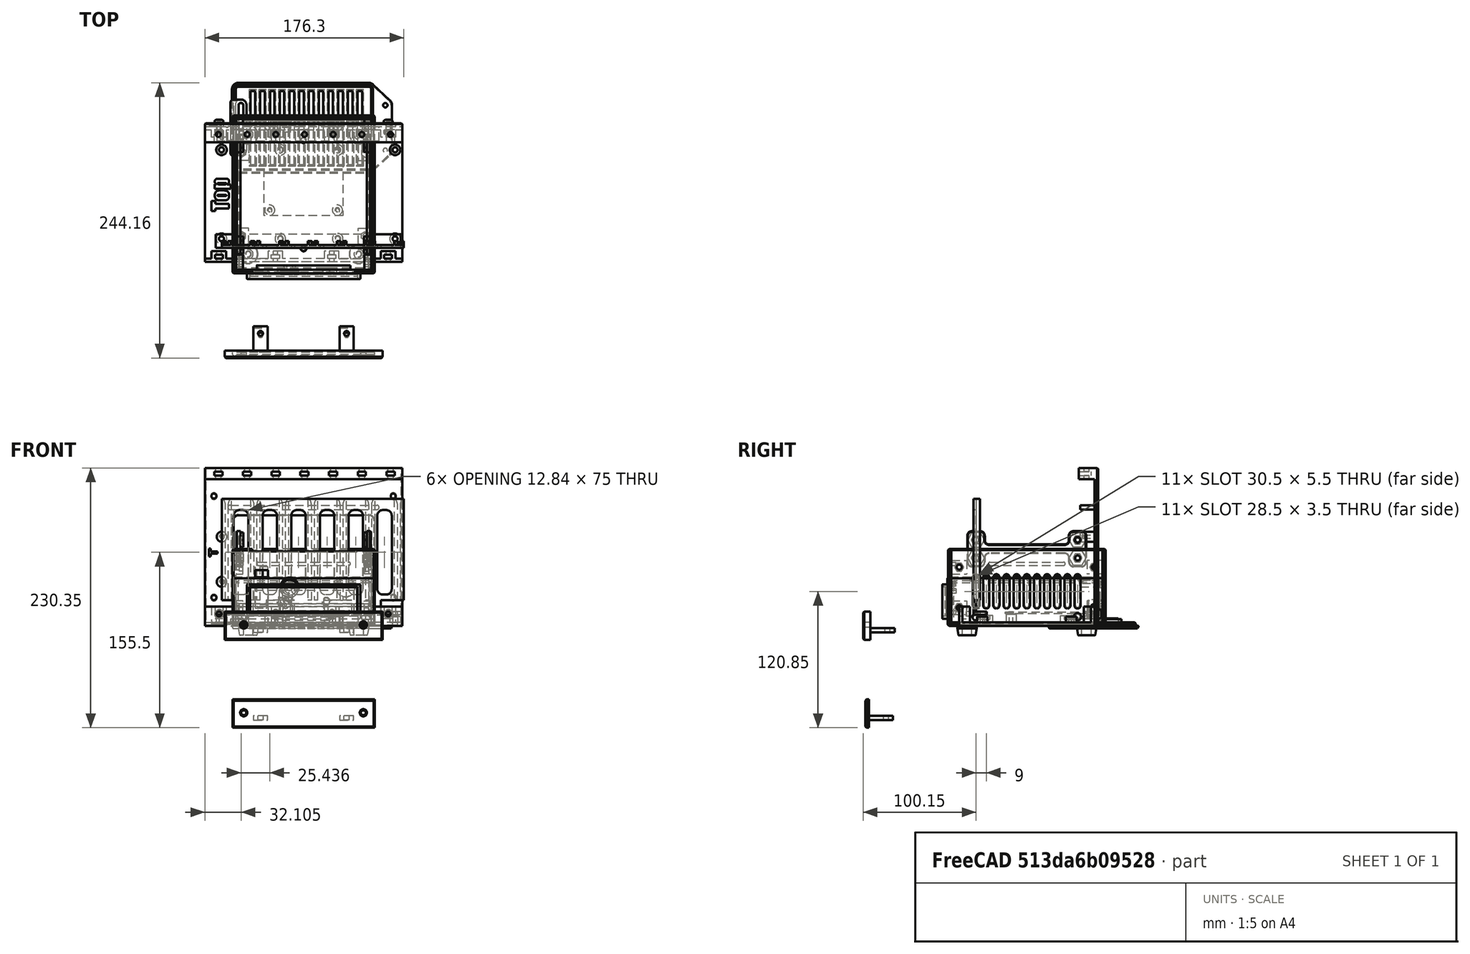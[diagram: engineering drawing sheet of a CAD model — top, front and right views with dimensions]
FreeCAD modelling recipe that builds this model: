
FCSTD DOCUMENT  (FreeCAD 0.20R29603 (Git))
Label: Assembly Model
License: All rights reserved
LicenseURL: http://en.wikipedia.org/wiki/All_rights_reserved
objects: Sketcher::SketchObject×60, PartDesign::Pocket×32, PartDesign::Pad×28, PartDesign::Chamfer×25, PartDesign::Body×14, PartDesign::Mirrored×12, Part::Feature×8, App::Part×6, PartDesign::Fillet×6, Part::FeaturePython×5, Part::Mirroring×4, App::DocumentObjectGroup×4, PartDesign::ShapeBinder×2, PartDesign::LinearPattern×1, PartDesign::Revolution×1, PartDesign::Thickness×1, Part::Part2DObjectPython×1
note: 293 computed .brp shape members not serialized (recipe doc carries the construction recipe); baked Part::Feature solids carry a one-line shape summary decoded from their .brp

FEATURE [Part::Feature] Part__Feature001  label="Guide"
  Placement = pos=(4.1875,39.425,9.65) rot=(0,0,1;0rad)
  shape: bbox 166.6 x 12 x 103 mm, 167 faces (baked)
FEATURE [Part::Mirroring] Part__Mirroring001  label="Guide (Mirror #2)"
  Base = (0,0,0)
  Normal = (0,1,0)
  Source = -> Part__Feature001
FEATURE [Part::Feature] Part__Feature004  label="M4 X 10 Pan Hd Pozi"
  Placement = pos=(-75,-63.15,10.5) rot=(1,0,0;1.5708rad)
  shape: bbox 8.444 x 13.1 x 8.444 mm, 27 faces (baked)
FEATURE [Part::FeaturePython] Array  # Draft array (typed FeaturePython)
  Angle = 360
  ArrayType = 0
  Axis = (0,0,1)
  Base = -> Part__Feature004
  Center = (0,0,0)
  Fuse = false
  IntervalAxis = (0,0,0)
  IntervalX = (50,0,0)
  IntervalY = (0,1,0)
  IntervalZ = (0,0,1)
  NumberPolar = 1
  NumberX = 4
  NumberY = 1
  NumberZ = 1
FEATURE [Part::Mirroring] Part__Mirroring003  label="Side panel retaining nuts"
  Base = (0,0,0)
  Normal = (0,1,0)
  Source = -> Array
FEATURE [Part::Feature] Part__Feature005  label="M4 Nut"
  Placement = pos=(-75,-55.375,10.5) rot=(1,0,0;0rad)
  shape: bbox 7.66 x 3.2 x 7.66 mm, 19 faces (baked)
FEATURE [Part::Feature] Part__Feature006  label="Sideplate"
  Placement = pos=(-8e-15,-63.1,0) rot=(0,0.707107,0.707107;3.14159rad)
  shape: bbox 175 x 17 x 140 mm, 120 faces (baked)
FEATURE [Part::Mirroring] Part__Mirroring  label="Sideplate (Mirror #5)"
  Base = (0,0,0)
  Normal = (0,1,0)
  Source = -> Part__Feature006
FEATURE [Part::Feature] Part__Feature007  label="Vented_cover"
  shape: bbox 142 x 80.02 x 8.7 mm, 193 faces (baked)
FEATURE [Part::Feature] Part__Feature008  label="Tab"
  shape: bbox 14.5 x 50 x 2.7 mm, 17 faces (baked)
FEATURE [App::DocumentObjectGroup] Group  label="Side-cover assy"
  Group = -> [Part__Feature007,Part__Feature008]
FEATURE [App::Part] Part  label="Side Cover Assy"
  Group = -> [Part__Feature008,Part__Feature007,Group]
  Origin = -> Origin002
  Placement = pos=(-7.7e-15,-63,0) rot=(0,0.707107,0.707107;3.14159rad)
FEATURE [Part::Feature] Part__Feature009  label="Tab001"
  shape: bbox 14.5 x 50 x 2.7 mm, 17 faces (baked)
FEATURE [Part::Feature] Part__Feature010  label="Vented_cover001"
  shape: bbox 142 x 80.02 x 8.7 mm, 193 faces (baked)
FEATURE [App::DocumentObjectGroup] Group001  label="Side-cover assy001"
  Group = -> [Part__Feature010,Part__Feature009]
FEATURE [App::Part] Part001  label="Side Cover Assy 2"
  Group = -> [Part__Feature009,Part__Feature010,Group001]
  Origin = -> Origin003
  Placement = pos=(7.7e-15,63,118) rot=(0,0.707107,-0.707107;3.14159rad)
FEATURE [Part::FeaturePython] Array001  label="Nuts for sideplate"  # Draft array (typed FeaturePython)
  Angle = 360
  ArrayType = 0
  Axis = (0,0,1)
  Base = -> Part__Feature005
  Center = (0,0,0)
  Fuse = false
  IntervalAxis = (0,0,0)
  IntervalX = (50,0,0)
  IntervalY = (0,1,0)
  IntervalZ = (0,0,1)
  NumberPolar = 1
  NumberX = 4
  NumberY = 1
  NumberZ = 1
FEATURE [Part::Mirroring] Part__Mirroring004  label="Nuts for sideplate (Mirror #5)"
  Base = (0,0,0)
  Normal = (0,1,0)
  Source = -> Array001
FEATURE [Sketcher::SketchObject] Sketch001  label="Base plate spec"
  FullyConstrained = false
  MapMode = 5
  Support = -> [XY_Plane005]
  sketch-geometry (12):
    g0: LineSegment StartX=-63 StartY=67 StartZ=0 EndX=63 EndY=67 EndZ=0
    g1: LineSegment StartX=63 StartY=67 StartZ=0 EndX=63 EndY=-67 EndZ=0
    g2: LineSegment StartX=63 StartY=-67 StartZ=0 EndX=-63 EndY=-67 EndZ=0
    g3: LineSegment StartX=-63 StartY=-67 StartZ=0 EndX=-63 EndY=67 EndZ=0
    g4: Circle CenterX=-49 CenterY=53 CenterZ=0 NormalX=0 NormalY=0 NormalZ=1 AngleXU=0 Radius=2.4
    g5: Circle CenterX=49 CenterY=53 CenterZ=0 NormalX=0 NormalY=0 NormalZ=1 AngleXU=0 Radius=2.4
    g6: Circle CenterX=-49 CenterY=-53 CenterZ=0 NormalX=0 NormalY=0 NormalZ=1 AngleXU=0 Radius=2.4
    g7: Circle CenterX=49 CenterY=-53 CenterZ=0 NormalX=0 NormalY=0 NormalZ=1 AngleXU=0 Radius=2.4
    g8: Circle CenterX=55 CenterY=37 CenterZ=0 NormalX=0 NormalY=0 NormalZ=1 AngleXU=0 Radius=2.4
    g9: Circle CenterX=-55 CenterY=37 CenterZ=0 NormalX=0 NormalY=0 NormalZ=1 AngleXU=0 Radius=2.4
    g10: Circle CenterX=-55 CenterY=-37 CenterZ=0 NormalX=0 NormalY=0 NormalZ=1 AngleXU=0 Radius=2.4
    g11: Circle CenterX=55 CenterY=-37 CenterZ=0 NormalX=0 NormalY=0 NormalZ=1 AngleXU=0 Radius=2.4
  constraints (28):
    c: Coincident(g0,g1)
    c: Coincident(g1,g2)
    c: Coincident(g2,g3)
    c: Coincident(g3,g0)
    c: Horizontal(g2)
    c: Vertical(g1)
    c: Symmetric(g0,g0,g-2)
    c: Symmetric(g0,g2,g-1)
    c: Distance(g0) = 126
    c: Distance(g3) = 134
    c: Radius(g4) = 2.4
    c: Equal(g4,g5)
    c: Equal(g4,g6)
    c: Equal(g4,g7)
    c: Symmetric(g4,g5,g-2)
    c: Symmetric(g4,g6,g-1)
    c: Symmetric(g7,g6,g-2)
    c: Distance(g4,g5) = 98
    c: DistanceY(g6,g4) = 106
    c: Symmetric(g10,g11,g-2)
    c: Symmetric(g9,g10,g-1)
    c: Symmetric(g9,g8,g-2)
    c: Radius(g9) = 2.4
    c: Equal(g9,g8)
    c: Equal(g9,g11)
    c: Equal(g9,g10)
    c: DistanceX(g0,g9) = 8
    c: DistanceY(g9,g0) = 30
FEATURE [PartDesign::Pad] Pad  label="Make base plate"
  AllowMultiFace = false
  Direction = (1,1,1)
  Length = 3
  Length2 = 100
  Profile = -> Sketch001
  Type = 0
FEATURE [Sketcher::SketchObject] Sketch002  label="Sideplate spec"
  FullyConstrained = false
  MapMode = 5
  Placement = pos=(0,0,0) rot=(1,0,0;1.5708rad)
  Support = -> [XZ_Plane006]
  sketch-geometry (4):
    g0: LineSegment StartX=-60 StartY=3.05 StartZ=0 EndX=-63 EndY=3.05 EndZ=0
    g1: LineSegment StartX=-63 StartY=3.05 StartZ=0 EndX=-63 EndY=68.05 EndZ=0
    g2: LineSegment StartX=-63 StartY=68.05 StartZ=0 EndX=-60 EndY=68.05 EndZ=0
    g3: LineSegment StartX=-60 StartY=68.05 StartZ=0 EndX=-60 EndY=3.05 EndZ=0
  constraints (12):
    c: Coincident(g0,g1)
    c: Coincident(g1,g2)
    c: Coincident(g2,g3)
    c: Horizontal(g0)
    c: Horizontal(g2)
    c: Vertical(g3)
    c: Vertical(g1)
    c: Distance(g1) = 65
    c: Distance(g2) = 3
    c: DistanceX(g0) = -63
    c: DistanceY(g0) = 3.05
    c: Coincident(g3,g0)
FEATURE [PartDesign::Pad] Pad001  label="Make sideplate"
  AllowMultiFace = false
  Direction = (1,1,1)
  Length = 134
  Length2 = 100
  Midplane = true
  Placement = pos=(0,0,0) rot=(1,0,0;1.5708rad)
  Profile = -> Sketch002
  Type = 0
FEATURE [Sketcher::SketchObject] Sketch003  label="Screwtab spec"
  ExternalGeometry = -> [Pad001]
  FullyConstrained = false
  MapMode = 5
  Placement = pos=(0,0,3.05) rot=(1,0,0;3.14159rad)
  Support = -> [Pad001]
  sketch-geometry (13):
    g0: LineSegment StartX=-60 StartY=44 StartZ=0 EndX=-48.5 EndY=44 EndZ=0
    g1: LineSegment StartX=-48.5 StartY=44 StartZ=0 EndX=-48.5 EndY=30 EndZ=0
    g2: LineSegment StartX=-48.5 StartY=30 StartZ=0 EndX=-60 EndY=30 EndZ=0
    g3: LineSegment StartX=-60 StartY=30 StartZ=0 EndX=-60 EndY=44 EndZ=0
    g4: LineSegment StartX=-60 StartY=37 StartZ=0 EndX=-48.5 EndY=37 EndZ=0
    g5: Circle CenterX=-55 CenterY=37 CenterZ=0 NormalX=0 NormalY=0 NormalZ=1 AngleXU=0 Radius=2.4
    g6: LineSegment StartX=-51.5 StartY=34.9793 StartZ=0 EndX=-51.5 EndY=39.0207 EndZ=0
    g7: LineSegment StartX=-51.5 StartY=39.0207 StartZ=0 EndX=-55 EndY=41.0415 EndZ=0
    g8: LineSegment StartX=-55 StartY=41.0415 StartZ=0 EndX=-58.5 EndY=39.0207 EndZ=0
    g9: LineSegment StartX=-58.5 StartY=39.0207 StartZ=0 EndX=-58.5 EndY=34.9793 EndZ=0
    g10: LineSegment StartX=-58.5 StartY=34.9793 StartZ=0 EndX=-55 EndY=32.9585 EndZ=0
    g11: LineSegment StartX=-55 StartY=32.9585 StartZ=0 EndX=-51.5 EndY=34.9793 EndZ=0
    g12: Circle CenterX=-55 CenterY=37 CenterZ=0 NormalX=0 NormalY=0 NormalZ=1 AngleXU=0 Radius=4.04145
  constraints (34):
    c: Coincident(g0,g1)
    c: Coincident(g1,g2)
    c: Coincident(g2,g3)
    c: Coincident(g3,g0)
    c: Horizontal(g0)
    c: Horizontal(g2)
    c: Vertical(g1)
    c: Vertical(g3)
    c: Perpendicular(g4,g1) = 4.71239
    c: PointOnObject(g4,g3)
    c: PointOnObject(g5,g4)
    c: PointOnObject(g0,g-3)
    c: Symmetric(g0,g1,g4)
    c: DistanceY(g5,g-3) = 30
    c: DistanceX(g-4,g5) = 8
    c: Coincident(g6,g7)
    c: Coincident(g7,g8)
    c: Coincident(g8,g9)
    c: Coincident(g9,g10)
    c: Coincident(g10,g11)
    c: Coincident(g11,g6)
    c: Equal(g6, g7-g11) x5
    c: PointOnObject(g6,g12)
    c: PointOnObject(g7,g12)
    c: PointOnObject(g8,g12)
    c: PointOnObject(g9,g12)
    c: PointOnObject(g10,g12)
    c: PointOnObject(g11,g12)
    c: Coincident(g12,g5)
    c: Vertical(g6)
    c: DistanceX(g9,g6) = 7
    c: DistanceX(g6,g0) = 3
    c: Distance(g1) = 14
    c: Radius(g5) = 2.4
FEATURE [PartDesign::Pad] Pad002  label="Add screwtab"
  AllowMultiFace = false
  BaseFeature = -> Pad001
  Direction = (1,1,1)
  Length = 6
  Length2 = 100
  Placement = pos=(0,0,0) rot=(1,0,0;1.5708rad)
  Profile = -> Sketch003
  Reversed = true
  Type = 0
FEATURE [PartDesign::Mirrored] Mirrored  label="Mirrored screwtab"
  BaseFeature = -> Pad002
  MirrorPlane = -> XZ_Plane006
  Originals = -> [Pad002]
  Placement = pos=(0,0,0) rot=(1,0,0;1.5708rad)
FEATURE [Sketcher::SketchObject] Sketch004  label="nut trap spec"
  ExternalGeometry = -> [Mirrored]
  FullyConstrained = false
  MapMode = 5
  Placement = pos=(0,-2e-15,9.05) rot=(0,0,1;3.14159rad)
  Support = -> [Mirrored]
  sketch-geometry (7):
    g0: LineSegment StartX=58.55 StartY=34.9504 StartZ=0 EndX=58.55 EndY=39.0496 EndZ=0
    g1: LineSegment StartX=58.55 StartY=39.0496 StartZ=0 EndX=55 EndY=41.0992 EndZ=0
    g2: LineSegment StartX=55 StartY=41.0992 StartZ=0 EndX=51.45 EndY=39.0496 EndZ=0
    g3: LineSegment StartX=51.45 StartY=39.0496 StartZ=0 EndX=51.45 EndY=34.9504 EndZ=0
    g4: LineSegment StartX=51.45 StartY=34.9504 StartZ=0 EndX=55 EndY=32.9008 EndZ=0
    g5: LineSegment StartX=55 StartY=32.9008 StartZ=0 EndX=58.55 EndY=34.9504 EndZ=0
    g6: Circle CenterX=55 CenterY=37 CenterZ=0 NormalX=0 NormalY=0 NormalZ=1 AngleXU=0 Radius=4.09919
  constraints (16):
    c: Coincident(g0,g1)
    c: Coincident(g1,g2)
    c: Coincident(g2,g3)
    c: Coincident(g3,g4)
    c: Coincident(g4,g5)
    c: Coincident(g5,g0)
    c: Equal(g0, g1-g5) x5
    c: PointOnObject(g0,g6)
    c: PointOnObject(g1,g6)
    c: PointOnObject(g2,g6)
    c: PointOnObject(g3,g6)
    c: PointOnObject(g4,g6)
    c: PointOnObject(g5,g6)
    c: Coincident(g6,g-3)
    c: Vertical(g0)
    c: Distance(g0,g3) = 7.1
FEATURE [PartDesign::Pocket] Pocket  label="Add nut trap"
  AllowMultiFace = false
  BaseFeature = -> Mirrored
  Direction = (1,1,1)
  Length = 3.5
  Length2 = 100
  Placement = pos=(0,0,0) rot=(1,0,0;1.5708rad)
  Profile = -> Sketch004
  Type = 0
FEATURE [PartDesign::Mirrored] Mirrored001  label="Mirrored nut-trap"
  BaseFeature = -> Pocket
  MirrorPlane = -> XZ_Plane006
  Originals = -> [Pocket]
  Placement = pos=(0,0,0) rot=(1,0,0;1.5708rad)
FEATURE [Sketcher::SketchObject] Sketch005  label="PCB Base"
  FullyConstrained = false
  MapMode = 5
  Support = -> [XY_Plane007]
  sketch-geometry (11):
    g0: LineSegment StartX=-50 StartY=35 StartZ=0 EndX=35 EndY=35 EndZ=0
    g1: LineSegment StartX=35 StartY=35 StartZ=0 EndX=35 EndY=-35 EndZ=0
    g2: LineSegment StartX=35 StartY=-35 StartZ=0 EndX=-50 EndY=-35 EndZ=0
    g3: LineSegment StartX=-50 StartY=-35 StartZ=0 EndX=-50 EndY=35 EndZ=0
    g4: Circle CenterX=-45 CenterY=-30 CenterZ=0 NormalX=0 NormalY=0 NormalZ=1 AngleXU=0 Radius=2.1
    g5: Circle CenterX=30 CenterY=-30 CenterZ=0 NormalX=0 NormalY=0 NormalZ=1 AngleXU=0 Radius=2.1
    g6: Circle CenterX=-45 CenterY=30 CenterZ=0 NormalX=0 NormalY=0 NormalZ=1 AngleXU=0 Radius=2.1
    g7: Circle CenterX=30 CenterY=30 CenterZ=0 NormalX=0 NormalY=0 NormalZ=1 AngleXU=0 Radius=2.1
    g8: LineSegment StartX=-7.5 StartY=35 StartZ=0 EndX=-7.5 EndY=-35 EndZ=0
    g9: LineSegment StartX=-50 StartY=-3.1e-15 StartZ=0 EndX=35 EndY=2.1e-15 EndZ=0
    g10: GeomPoint X=0 Y=0 Z=0
  constraints (28):
    c: Coincident(g0,g1)
    c: Coincident(g1,g2)
    c: Coincident(g2,g3)
    c: Coincident(g3,g0)
    c: Horizontal(g0)
    c: Horizontal(g2)
    c: Vertical(g1)
    c: Vertical(g3)
    c: Distance(g3) = 70
    c: Distance(g0) = 85
    c: Radius(g6) = 2.1
    c: Equal(g6,g7)
    c: Equal(g6,g4)
    c: Equal(g6,g5)
    c: Perpendicular(g9,g3) = 1.5708
    c: Perpendicular(g8,g0) = 1.5708
    c: PointOnObject(g8,g2)
    c: PointOnObject(g9,g1)
    c: Symmetric(g2,g0,g9)
    c: Symmetric(g0,g0,g8)
    c: Symmetric(g6,g7,g8)
    c: Symmetric(g4,g6,g9)
    c: Symmetric(g4,g5,g8)
    c: DistanceX(g2,g4) = 5
    c: DistanceY(g2,g4) = 5
    c: Coincident(g10,g-1)
    c: PointOnObject(g10,g9)
    c: DistanceX(g0) = 35
FEATURE [PartDesign::Pad] Pad003  label="Make PCB Laminate"
  AllowMultiFace = false
  Direction = (1,1,1)
  Length = 1.6
  Length2 = 100
  Profile = -> Sketch005
  Type = 0
FEATURE [Sketcher::SketchObject] Sketch006  label="DCJack footprint"
  ExternalGeometry = -> [Pad003]
  FullyConstrained = false
  MapMode = 5
  Placement = pos=(0,0,1.6) rot=(0,0,1;0rad)
  Support = -> [Pad003]
  sketch-geometry (7):
    g0: LineSegment StartX=23.95 StartY=20.45 StartZ=0 EndX=38 EndY=20.45 EndZ=0
    g1: LineSegment StartX=38 StartY=20.45 StartZ=0 EndX=38 EndY=11.45 EndZ=0
    g2: LineSegment StartX=38 StartY=11.45 StartZ=0 EndX=23.95 EndY=11.45 EndZ=0
    g3: LineSegment StartX=23.95 StartY=11.45 StartZ=0 EndX=23.95 EndY=20.45 EndZ=0
    g4: LineSegment StartX=38 StartY=15.95 StartZ=0 EndX=23.95 EndY=15.95 EndZ=0
    g5: LineSegment StartX=30.975 StartY=20.45 StartZ=0 EndX=30.975 EndY=11.45 EndZ=0
    g6: GeomPoint X=30.975 Y=15.95 Z=0
  constraints (19):
    c: Coincident(g0,g1)
    c: Coincident(g1,g2)
    c: Coincident(g2,g3)
    c: Coincident(g3,g0)
    c: Horizontal(g0)
    c: Horizontal(g2)
    c: Vertical(g1)
    c: Distance(g1) = 9
    c: Distance(g2) = 14.05
    c: Perpendicular(g4,g1) = 1.5708
    c: PointOnObject(g4,g3)
    c: Perpendicular(g5,g0) = 1.5708
    c: PointOnObject(g5,g2)
    c: Symmetric(g0,g0,g5)
    c: Symmetric(g2,g0,g4)
    c: PointOnObject(g6,g5)
    c: PointOnObject(g6,g4)
    c: DistanceY(g6,g-3) = 19.05
    c: DistanceX(g-3,g0) = 3
FEATURE [PartDesign::Pad] Pad004  label="DC Jack block"
  AllowMultiFace = false
  BaseFeature = -> Pad003
  Direction = (1,1,1)
  Length = 11
  Length2 = 100
  Profile = -> Sketch006
  Type = 0
FEATURE [Sketcher::SketchObject] Sketch007  label="hole and pin spec"
  ExternalGeometry = -> [Pad004]
  FullyConstrained = false
  MapMode = 5
  Placement = pos=(38,0,0) rot=(0.57735,0.57735,0.57735;2.0944rad)
  Support = -> [Pad004]
  sketch-geometry (3):
    g0: Circle CenterX=15.95 CenterY=8.1 CenterZ=0 NormalX=0 NormalY=0 NormalZ=1 AngleXU=0 Radius=3.25
    g1: LineSegment StartX=15.95 StartY=12.6 StartZ=0 EndX=15.95 EndY=11.35 EndZ=0
    g2: Circle CenterX=15.95 CenterY=8.1 CenterZ=0 NormalX=0 NormalY=0 NormalZ=1 AngleXU=0 Radius=1.05
  constraints (7):
    c: Perpendicular(g1,g0) = 4.71239
    c: Perpendicular(g1,g-3) = 4.71239
    c: Symmetric(g-3,g-3,g1)
    c: Radius(g0) = 3.25
    c: Distance(g1) = 1.25
    c: Coincident(g2,g0)
    c: Radius(g2) = 1.05
FEATURE [PartDesign::Pocket] Pocket001  label="Make hole and pin spec"
  AllowMultiFace = false
  BaseFeature = -> Pad004
  Direction = (1,1,1)
  Length = 9.5
  Length2 = 100
  Profile = -> Sketch007
  Type = 0
FEATURE [PartDesign::Fillet] Fillet001  label="Finish pin"
  Base = -> Pocket001 [Edge46]
  BaseFeature = -> Pocket001
  Radius = 0.5
  SupportTransform = false
  UseAllEdges = false
FEATURE [Sketcher::SketchObject] Sketch008  label="Unneccesary back face decor"
  ExternalGeometry = -> [Fillet001]
  FullyConstrained = false
  MapMode = 5
  Placement = pos=(23.95,0,0) rot=(0.57735,-0.57735,-0.57735;2.0944rad)
  Support = -> [Fillet001]
  sketch-geometry (5):
    g0: ArcOfCircle CenterX=-15.95 CenterY=7.95 CenterZ=0 NormalX=0 NormalY=0 NormalZ=1 AngleXU=0 Radius=4.5 StartAngle=0 EndAngle=3.14159
    g1: LineSegment StartX=-20.45 StartY=7.95 StartZ=0 EndX=-20.45 EndY=12.6 EndZ=0
    g2: LineSegment StartX=-20.45 StartY=12.6 StartZ=0 EndX=-11.45 EndY=12.6 EndZ=0
    g3: LineSegment StartX=-11.45 StartY=12.6 StartZ=0 EndX=-11.45 EndY=7.95 EndZ=0
    g4: LineSegment StartX=-15.95 StartY=12.45 StartZ=0 EndX=-15.95 EndY=12.6 EndZ=0
  constraints (11):
    c: Coincident(g1,g2)
    c: Coincident(g2,g3)
    c: Vertical(g3)
    c: Vertical(g1)
    c: Coincident(g1,g-5)
    c: Coincident(g2,g-4)
    c: Tangent(g0,g3) = 1.5708
    c: Tangent(g1,g0) = 1.5708
    c: Perpendicular(g4,g2) = 4.71239
    c: Perpendicular(g4,g0) = 1.5708
    c: Distance(g4) = 0.15
FEATURE [PartDesign::Pocket] Pocket002  label="Add jack back decor"
  AllowMultiFace = false
  BaseFeature = -> Fillet001
  Direction = (1,1,1)
  Length = 10
  Length2 = 100
  Profile = -> Sketch008
  Type = 0
FEATURE [PartDesign::Body] Body003  label="PCB"
  Group = -> [Sketch005,Pad003,Sketch006,Pad004,Sketch007,Pocket001,Fillet001,Sketch008,Pocket002]
  Origin = -> Origin007
  Placement = pos=(0,31,10.6) rot=(0,0,1;1.5708rad)
  Tip = -> Pocket002
FEATURE [Sketcher::SketchObject] Sketch009  label="PCB Mounting pillar spec"
  FullyConstrained = false
  MapMode = 5
  Placement = pos=(0,0,3) rot=(0,0,1;0rad)
  Support = -> [Pad]
  sketch-geometry (10):
    g0: LineSegment StartX=-30 StartY=61 StartZ=0 EndX=30 EndY=61 EndZ=0
    g1: LineSegment StartX=30 StartY=61 StartZ=0 EndX=30 EndY=-14 EndZ=0
    g2: LineSegment StartX=30 StartY=-14 StartZ=0 EndX=-30 EndY=-14 EndZ=0
    g3: LineSegment StartX=-30 StartY=-14 StartZ=0 EndX=-30 EndY=61 EndZ=0
    g4: Circle CenterX=-30 CenterY=61 CenterZ=0 NormalX=0 NormalY=0 NormalZ=1 AngleXU=0 Radius=4.5
    g5: Circle CenterX=30 CenterY=61 CenterZ=0 NormalX=0 NormalY=0 NormalZ=1 AngleXU=0 Radius=4.5
    g6: Circle CenterX=-30 CenterY=-14 CenterZ=0 NormalX=0 NormalY=0 NormalZ=1 AngleXU=0 Radius=4.5
    g7: Circle CenterX=30 CenterY=-14 CenterZ=0 NormalX=0 NormalY=0 NormalZ=1 AngleXU=0 Radius=4.5
    g8: LineSegment StartX=-2.3e-15 StartY=61 StartZ=0 EndX=2.3e-15 EndY=-14 EndZ=0
    g9: LineSegment StartX=-30 StartY=23.5 StartZ=0 EndX=0 EndY=23.5 EndZ=0
  constraints (26):
    c: Coincident(g0,g1)
    c: Coincident(g1,g2)
    c: Coincident(g2,g3)
    c: Coincident(g3,g0)
    c: Horizontal(g0)
    c: Horizontal(g2)
    c: Vertical(g1)
    c: Vertical(g3)
    c: Distance(g0) = 60
    c: Distance(g3) = 75
    c: Coincident(g6,g2)
    c: Coincident(g7,g1)
    c: Coincident(g5,g0)
    c: Coincident(g4,g0)
    c: Radius(g4) = 4.5
    c: Equal(g4,g5)
    c: Equal(g4,g7)
    c: Equal(g4,g6)
    c: Perpendicular(g9,g3) = 1.5708
    c: Perpendicular(g8,g0) = 1.5708
    c: PointOnObject(g9,g8)
    c: PointOnObject(g8,g2)
    c: Symmetric(g5,g4,g8)
    c: Symmetric(g6,g4,g9)
    c: PointOnObject(g9,g-2)
    c: DistanceY(g4) = 61
FEATURE [PartDesign::Pad] Pad005  label="Add PCB Mounting pillars 7.4 high"
  AllowMultiFace = false
  BaseFeature = -> Pad
  Direction = (1,1,1)
  Length = 7.4
  Length2 = 100
  Profile = -> Sketch009
  Type = 0
FEATURE [Sketcher::SketchObject] Sketch010  label="PCB Screwhole spec"
  ExternalGeometry = -> [Pad005]
  FullyConstrained = false
  MapMode = 5
  Placement = pos=(0,0,10.4) rot=(0,0,1;0rad)
  Support = -> [Pad005]
  sketch-geometry (4):
    g0: Circle CenterX=-30 CenterY=61 CenterZ=0 NormalX=0 NormalY=0 NormalZ=1 AngleXU=0 Radius=1.5
    g1: Circle CenterX=30 CenterY=61 CenterZ=0 NormalX=0 NormalY=0 NormalZ=1 AngleXU=0 Radius=1.5
    g2: Circle CenterX=30 CenterY=-14 CenterZ=0 NormalX=0 NormalY=0 NormalZ=1 AngleXU=0 Radius=1.5
    g3: Circle CenterX=-30 CenterY=-14 CenterZ=0 NormalX=0 NormalY=0 NormalZ=1 AngleXU=0 Radius=1.5
  constraints (8):
    c: Radius(g0) = 1.5
    c: Equal(g0,g1)
    c: Equal(g0,g2)
    c: Equal(g0,g3)
    c: Coincident(g3,g-6)
    c: Coincident(g2,g-5)
    c: Coincident(g0,g-3)
    c: Coincident(g1,g-4)
FEATURE [Sketcher::SketchObject] Sketch011  label="Front Endplate spec"
  FullyConstrained = false
  MapMode = 5
  Placement = pos=(0,0,0) rot=(1,0,0;1.5708rad)
  Support = -> [XZ_Plane008]
  sketch-geometry (4):
    g0: LineSegment StartX=-63 StartY=68 StartZ=0 EndX=63 EndY=68 EndZ=0
    g1: LineSegment StartX=63 StartY=68 StartZ=0 EndX=63 EndY=0 EndZ=0
    g2: LineSegment StartX=63 StartY=0 StartZ=0 EndX=-63 EndY=0 EndZ=0
    g3: LineSegment StartX=-63 StartY=0 StartZ=0 EndX=-63 EndY=68 EndZ=0
  constraints (11):
    c: Coincident(g0,g1)
    c: Coincident(g1,g2)
    c: Coincident(g2,g3)
    c: Coincident(g3,g0)
    c: Horizontal(g2)
    c: Vertical(g1)
    c: Vertical(g3)
    c: Distance(g0) = 126
    c: Symmetric(g0,g0,g-2)
    c: Distance(g3) = 68
    c: PointOnObject(g2,g-1)
FEATURE [PartDesign::Pad] Pad006  label="Make front endplate"
  AllowMultiFace = false
  Direction = (1,1,1)
  Length = 3
  Length2 = 100
  Placement = pos=(0,0,0) rot=(1,0,0;1.5708rad)
  Profile = -> Sketch011
  Type = 0
FEATURE [Sketcher::SketchObject] Sketch012  label="Endplate mounting blocks"
  ExternalGeometry = -> [Pad006]
  FullyConstrained = false
  MapMode = 5
  Placement = pos=(0,-1e-16,0) rot=(-1,0,0;1.5708rad)
  Support = -> [Pad006]
  sketch-geometry (9):
    g0: LineSegment StartX=-59.85 StartY=-10 StartZ=0 EndX=-53.85 EndY=-10 EndZ=0
    g1: LineSegment StartX=-53.85 StartY=-10 StartZ=0 EndX=-53.85 EndY=-22 EndZ=0
    g2: LineSegment StartX=-53.85 StartY=-22 StartZ=0 EndX=-59.85 EndY=-22 EndZ=0
    g3: LineSegment StartX=-59.85 StartY=-22 StartZ=0 EndX=-59.85 EndY=-10 EndZ=0
    g4: LineSegment StartX=-59.85 StartY=-46 StartZ=0 EndX=-53.85 EndY=-46 EndZ=0
    g5: LineSegment StartX=-53.85 StartY=-46 StartZ=0 EndX=-53.85 EndY=-58 EndZ=0
    g6: LineSegment StartX=-53.85 StartY=-58 StartZ=0 EndX=-59.85 EndY=-58 EndZ=0
    g7: LineSegment StartX=-59.85 StartY=-58 StartZ=0 EndX=-59.85 EndY=-46 EndZ=0
    g8: LineSegment StartX=-59.85 StartY=-22 StartZ=0 EndX=-59.85 EndY=-46 EndZ=0
  constraints (26):
    c: Coincident(g0,g1)
    c: Coincident(g1,g2)
    c: Coincident(g2,g3)
    c: Coincident(g3,g0)
    c: Horizontal(g0)
    c: Horizontal(g2)
    c: Vertical(g1)
    c: Vertical(g3)
    c: Coincident(g4,g5)
    c: Coincident(g5,g6)
    c: Coincident(g6,g7)
    c: Coincident(g7,g4)
    c: Horizontal(g4)
    c: Horizontal(g6)
    c: Vertical(g5)
    c: Vertical(g7)
    c: Equal(g0,g4)
    c: Equal(g5,g1)
    c: Distance(g0) = 6
    c: DistanceY(g0) = -10
    c: DistanceY(g-3,g6) = 10
    c: DistanceX(g-3,g6) = 3.15
    c: Coincident(g4,g8)
    c: Vertical(g8)
    c: Coincident(g8,g2)
    c: Distance(g1) = 12
FEATURE [PartDesign::Pad] Pad007
  AllowMultiFace = false
  BaseFeature = -> Pad006
  Direction = (1,1,1)
  Length = 13.5
  Length2 = 100
  Placement = pos=(0,0,0) rot=(1,0,0;1.5708rad)
  Profile = -> Sketch012
  Type = 0
FEATURE [PartDesign::Mirrored] Mirrored002
  BaseFeature = -> Pad007
  MirrorPlane = -> YZ_Plane008
  Originals = -> [Pad007]
  Placement = pos=(0,0,0) rot=(1,0,0;1.5708rad)
FEATURE [Sketcher::SketchObject] Sketch013  label="Side mounting hole spec"
  ExternalGeometry = -> [Mirrored002]
  FullyConstrained = false
  MapMode = 5
  Placement = pos=(59.85,-1.32e-14,1.32e-14) rot=(0.707107,0,0.707107;3.14159rad)
  Support = -> [Mirrored002]
  sketch-geometry (6):
    g0: Circle CenterX=16 CenterY=-7 CenterZ=0 NormalX=0 NormalY=0 NormalZ=1 AngleXU=0 Radius=2.25
    g1: Circle CenterX=52 CenterY=-7 CenterZ=0 NormalX=0 NormalY=0 NormalZ=1 AngleXU=0 Radius=2.25
    g2: LineSegment StartX=52 StartY=-7 StartZ=0 EndX=52 EndY=-13.5 EndZ=0
    g3: LineSegment StartX=52 StartY=-7 StartZ=0 EndX=58 EndY=-7 EndZ=0
    g4: LineSegment StartX=52 StartY=-7 StartZ=0 EndX=16 EndY=-7 EndZ=0
    g5: LineSegment StartX=16 StartY=-7 StartZ=0 EndX=16 EndY=-13.5 EndZ=0
  constraints (15):
    c: Coincident(g2,g1)
    c: Coincident(g2,g3)
    c: Horizontal(g3)
    c: PointOnObject(g2,g-5)
    c: Symmetric(g-6,g-5,g2)
    c: PointOnObject(g3,g-6)
    c: DistanceY(g3,g-6) = 7
    c: Coincident(g4,g1)
    c: Coincident(g4,g0)
    c: Horizontal(g4)
    c: Coincident(g5,g0)
    c: Perpendicular(g5,g-3) = 4.71239
    c: Symmetric(g-3,g-4,g5)
    c: Radius(g0) = 2.25
    c: Equal(g0,g1)
FEATURE [PartDesign::Pocket] Pocket004  label="Add side mounting holes001"
  AllowMultiFace = false
  BaseFeature = -> Mirrored002
  Direction = (1,1,1)
  Length = 5
  Length2 = 100
  Placement = pos=(0,0,0) rot=(1,0,0;1.5708rad)
  Profile = -> Sketch013
  Type = 1
FEATURE [Sketcher::SketchObject] Sketch014  label="Nut trap spec"
  ExternalGeometry = -> [Pocket004]
  FullyConstrained = false
  MapMode = 5
  Placement = pos=(-53.85,0,0) rot=(0.707107,0,0.707107;3.14159rad)
  Support = -> [Pocket004]
  sketch-geometry (14):
    g0: LineSegment StartX=19.5 StartY=-9.02073 StartZ=0 EndX=19.5 EndY=-4.97927 EndZ=0
    g1: LineSegment StartX=19.5 StartY=-4.97927 StartZ=0 EndX=16 EndY=-2.95855 EndZ=0
    g2: LineSegment StartX=16 StartY=-2.95855 StartZ=0 EndX=12.5 EndY=-4.97927 EndZ=0
    g3: LineSegment StartX=12.5 StartY=-4.97927 StartZ=0 EndX=12.5 EndY=-9.02073 EndZ=0
    g4: LineSegment StartX=12.5 StartY=-9.02073 StartZ=0 EndX=16 EndY=-11.0415 EndZ=0
    g5: LineSegment StartX=16 StartY=-11.0415 StartZ=0 EndX=19.5 EndY=-9.02073 EndZ=0
    g6: Circle CenterX=16 CenterY=-7 CenterZ=0 NormalX=0 NormalY=0 NormalZ=1 AngleXU=0 Radius=4.04145
    g7: LineSegment StartX=55.5 StartY=-9.02073 StartZ=0 EndX=55.5 EndY=-4.97927 EndZ=0
    g8: LineSegment StartX=55.5 StartY=-4.97927 StartZ=0 EndX=52 EndY=-2.95855 EndZ=0
    g9: LineSegment StartX=52 StartY=-2.95855 StartZ=0 EndX=48.5 EndY=-4.97927 EndZ=0
    g10: LineSegment StartX=48.5 StartY=-4.97927 StartZ=0 EndX=48.5 EndY=-9.02073 EndZ=0
    g11: LineSegment StartX=48.5 StartY=-9.02073 StartZ=0 EndX=52 EndY=-11.0415 EndZ=0
    g12: LineSegment StartX=52 StartY=-11.0415 StartZ=0 EndX=55.5 EndY=-9.02073 EndZ=0
    g13: Circle CenterX=52 CenterY=-7 CenterZ=0 NormalX=0 NormalY=0 NormalZ=1 AngleXU=0 Radius=4.04145
  constraints (32):
    c: Coincident(g0,g1)
    c: Coincident(g1,g2)
    c: Coincident(g2,g3)
    c: Coincident(g3,g4)
    c: Coincident(g4,g5)
    c: Coincident(g5,g0)
    c: Equal(g0, g1-g5) x5
    c: PointOnObject(g0,g6)
    c: PointOnObject(g1,g6)
    c: PointOnObject(g2,g6)
    c: PointOnObject(g3,g6)
    c: PointOnObject(g4,g6)
    c: PointOnObject(g5,g6)
    c: Coincident(g7,g8)
    c: Coincident(g8,g9)
    c: Coincident(g9,g10)
    c: Coincident(g10,g11)
    c: Coincident(g11,g12)
    c: Coincident(g12,g7)
    c: Equal(g7, g8-g12) x5
    c: PointOnObject(g7,g13)
    c: PointOnObject(g8,g13)
    c: PointOnObject(g9,g13)
    c: PointOnObject(g10,g13)
    c: PointOnObject(g11,g13)
    c: PointOnObject(g12,g13)
    c: Vertical(g0)
    c: Vertical(g7)
    c: Coincident(g6,g-3)
    c: Coincident(g13,g-4)
    c: Distance(g2,g0) = 7
    c: Equal(g13,g6)
FEATURE [PartDesign::Pocket] Pocket005  label="Add nut trap to side mounting lugs"
  AllowMultiFace = false
  BaseFeature = -> Pocket004
  Direction = (1,1,1)
  Length = 3.5
  Length2 = 100
  Placement = pos=(0,0,0) rot=(1,0,0;1.5708rad)
  Profile = -> Sketch014
  Type = 0
FEATURE [Sketcher::SketchObject] Sketch015  label="Side mounting screwhole spec one end"
  ExternalGeometry = -> [Mirrored001]
  FullyConstrained = false
  MapMode = 5
  Placement = pos=(-63,0,0) rot=(0.707107,0,-0.707107;3.14159rad)
  Support = -> [Mirrored001]
  sketch-geometry (3):
    g0: Circle CenterX=-16 CenterY=59.9 CenterZ=0 NormalX=0 NormalY=0 NormalZ=1 AngleXU=0 Radius=2.25
    g1: Circle CenterX=-52.05 CenterY=59.9 CenterZ=0 NormalX=0 NormalY=0 NormalZ=1 AngleXU=0 Radius=2.25
    g2: LineSegment StartX=-52.05 StartY=59.9 StartZ=0 EndX=-16 EndY=59.9 EndZ=0
  constraints (8):
    c: Radius(g1) = 2.25
    c: Equal(g1,g0)
    c: Horizontal(g2)
    c: Coincident(g2,g1)
    c: Coincident(g2,g0)
    c: DistanceX(g0,g-3) = 12.95
    c: DistanceX(g-3,g1) = 16
    c: DistanceY(g0,g-3) = 7.1
FEATURE [PartDesign::Pocket] Pocket006  label="Add one end side-mounting screwholes"
  AllowMultiFace = false
  BaseFeature = -> Mirrored001
  Direction = (1,1,1)
  Length = 5
  Length2 = 100
  Placement = pos=(0,0,0) rot=(1,0,0;1.5708rad)
  Profile = -> Sketch015
  Type = 1
FEATURE [PartDesign::Mirrored] Mirrored003  label="side mounting holes Mirrored"
  BaseFeature = -> Pocket006
  MirrorPlane = -> XZ_Plane006
  Originals = -> [Pocket006]
  Placement = pos=(0,0,0) rot=(1,0,0;1.5708rad)
FEATURE [Sketcher::SketchObject] Sketch016  label="Base to main-box interface hole spec"
  ExternalGeometry = -> [Mirrored003]
  FullyConstrained = false
  MapMode = 5
  Placement = pos=(-60,0,0) rot=(0.707107,0,0.707107;3.14159rad)
  Support = -> [Mirrored003]
  sketch-geometry (2):
    g0: Circle CenterX=60.05 CenterY=45 CenterZ=0 NormalX=0 NormalY=0 NormalZ=1 AngleXU=0 Radius=2.25
    g1: Circle CenterX=60.05 CenterY=-45 CenterZ=0 NormalX=0 NormalY=0 NormalZ=1 AngleXU=0 Radius=2.25
  constraints (5):
    c: Symmetric(g1,g0,g-1)
    c: Radius(g0) = 2.25
    c: Equal(g0,g1)
    c: DistanceY(g0,g-3) = 22
    c: DistanceX(g0,g-3) = 8
FEATURE [PartDesign::Pocket] Pocket007  label="Base to mainbox interface holes"
  AllowMultiFace = false
  BaseFeature = -> Mirrored003
  Direction = (1,1,1)
  Length = 5
  Length2 = 100
  Placement = pos=(0,0,0) rot=(1,0,0;1.5708rad)
  Profile = -> Sketch016
  Type = 1
FEATURE [Sketcher::SketchObject] Sketch017  label="Grille slot"
  FullyConstrained = false
  MapMode = 5
  Placement = pos=(-63,0,0) rot=(0.707107,0,-0.707107;3.14159rad)
  Support = -> [Pocket007]
  sketch-geometry (4):
    g0: ArcOfCircle CenterX=-43 CenterY=45 CenterZ=0 NormalX=0 NormalY=0 NormalZ=1 AngleXU=0 Radius=1.75 StartAngle=1.5708 EndAngle=4.71239
    g1: ArcOfCircle CenterX=-18 CenterY=45 CenterZ=0 NormalX=0 NormalY=0 NormalZ=1 AngleXU=0 Radius=1.75 StartAngle=4.71239 EndAngle=7.85398
    g2: LineSegment StartX=-43 StartY=43.25 StartZ=0 EndX=-18 EndY=43.25 EndZ=0
    g3: LineSegment StartX=-43 StartY=46.75 StartZ=0 EndX=-18 EndY=46.75 EndZ=0
  constraints (10):
    c: Tangent(g0,g3) = 1.5708
    c: Tangent(g0,g2) = -1.5708
    c: Tangent(g2,g1) = -1.5708
    c: Tangent(g3,g1) = 1.5708
    c: Equal(g0,g1)
    c: Distance(g0,g0) = 3.5
    c: Distance(g3) = 25
    c: DistanceX(g1) = -18
    c: DistanceY(g1) = 45
    c: Horizontal(g3)
FEATURE [PartDesign::Pocket] Pocket008  label="Add grille slot"
  AllowMultiFace = false
  BaseFeature = -> Pocket007
  Direction = (1,1,1)
  Length = 5
  Length2 = 100
  Placement = pos=(0,0,0) rot=(1,0,0;1.5708rad)
  Profile = -> Sketch017
  Type = 1
FEATURE [PartDesign::LinearPattern] LinearPattern  label="Make grille pattern"
  BaseFeature = -> Pocket008
  Direction = -> Sketch017 [V_Axis]
  Length = 90
  Occurrences = 11
  Originals = -> [Pocket008]
  Placement = pos=(0,0,0) rot=(1,0,0;1.5708rad)
  Reversed = true
FEATURE [PartDesign::Chamfer] Chamfer001  label="Grille Chamfer"
  Angle = 45
  Base = -> LinearPattern [Edge106,Edge103,Edge97,Edge93,Edge85,Edge89,Edge81,Edge125,Edge121,Edge112,Edge116]
  BaseFeature = -> LinearPattern
  ChamferType = 0
  FlipDirection = false
  Placement = pos=(0,0,0) rot=(1,0,0;1.5708rad)
  Size = 1
  Size2 = 1
  SupportTransform = false
  UseAllEdges = false
FEATURE [Sketcher::SketchObject] Sketch018  label="Rear endplate spec"
  FullyConstrained = false
  MapMode = 5
  Placement = pos=(0,0,0) rot=(1,0,0;1.5708rad)
  Support = -> [XZ_Plane009]
  sketch-geometry (4):
    g0: LineSegment StartX=-63 StartY=68 StartZ=0 EndX=63 EndY=68 EndZ=0
    g1: LineSegment StartX=63 StartY=68 StartZ=0 EndX=63 EndY=0 EndZ=0
    g2: LineSegment StartX=63 StartY=0 StartZ=0 EndX=-63 EndY=0 EndZ=0
    g3: LineSegment StartX=-63 StartY=0 StartZ=0 EndX=-63 EndY=68 EndZ=0
  constraints (11):
    c: Coincident(g0,g1)
    c: Coincident(g1,g2)
    c: Coincident(g2,g3)
    c: Coincident(g3,g0)
    c: Horizontal(g2)
    c: Vertical(g1)
    c: Vertical(g3)
    c: Distance(g0) = 126
    c: Symmetric(g0,g0,g-2)
    c: Distance(g3) = 68
    c: PointOnObject(g2,g-1)
FEATURE [PartDesign::Pad] Pad008  label="Make rear endplate"
  AllowMultiFace = false
  Direction = (1,1,1)
  Length = 3
  Length2 = 100
  Placement = pos=(0,0,0) rot=(1,0,0;1.5708rad)
  Profile = -> Sketch018
  Type = 0
FEATURE [Sketcher::SketchObject] Sketch019  label="Rear endplate mounting blocks"
  ExternalGeometry = -> [Pad008]
  FullyConstrained = false
  MapMode = 5
  Placement = pos=(0,-1e-16,0) rot=(-1,0,0;1.5708rad)
  Support = -> [Pad008]
  sketch-geometry (9):
    g0: LineSegment StartX=-59.85 StartY=-10 StartZ=0 EndX=-53.85 EndY=-10 EndZ=0
    g1: LineSegment StartX=-53.85 StartY=-10 StartZ=0 EndX=-53.85 EndY=-22 EndZ=0
    g2: LineSegment StartX=-53.85 StartY=-22 StartZ=0 EndX=-59.85 EndY=-22 EndZ=0
    g3: LineSegment StartX=-59.85 StartY=-22 StartZ=0 EndX=-59.85 EndY=-10 EndZ=0
    g4: LineSegment StartX=-59.85 StartY=-46 StartZ=0 EndX=-53.85 EndY=-46 EndZ=0
    g5: LineSegment StartX=-53.85 StartY=-46 StartZ=0 EndX=-53.85 EndY=-58 EndZ=0
    g6: LineSegment StartX=-53.85 StartY=-58 StartZ=0 EndX=-59.85 EndY=-58 EndZ=0
    g7: LineSegment StartX=-59.85 StartY=-58 StartZ=0 EndX=-59.85 EndY=-46 EndZ=0
    g8: LineSegment StartX=-59.85 StartY=-22 StartZ=0 EndX=-59.85 EndY=-46 EndZ=0
  constraints (26):
    c: Coincident(g0,g1)
    c: Coincident(g1,g2)
    c: Coincident(g2,g3)
    c: Coincident(g3,g0)
    c: Horizontal(g0)
    c: Horizontal(g2)
    c: Vertical(g1)
    c: Vertical(g3)
    c: Coincident(g4,g5)
    c: Coincident(g5,g6)
    c: Coincident(g6,g7)
    c: Coincident(g7,g4)
    c: Horizontal(g4)
    c: Horizontal(g6)
    c: Vertical(g5)
    c: Vertical(g7)
    c: Equal(g0,g4)
    c: Equal(g5,g1)
    c: Distance(g0) = 6
    c: DistanceY(g0) = -10
    c: DistanceY(g-3,g6) = 10
    c: DistanceX(g-3,g6) = 3.15
    c: Coincident(g4,g8)
    c: Vertical(g8)
    c: Coincident(g8,g2)
    c: Distance(g1) = 12
FEATURE [PartDesign::Pad] Pad009  label="Add rear endplate mounting blocks"
  AllowMultiFace = false
  BaseFeature = -> Pad008
  Direction = (1,1,1)
  Length = 13.5
  Length2 = 100
  Placement = pos=(0,0,0) rot=(1,0,0;1.5708rad)
  Profile = -> Sketch019
  Type = 0
FEATURE [PartDesign::Mirrored] Mirrored004
  BaseFeature = -> Pad009
  MirrorPlane = -> YZ_Plane009
  Originals = -> [Pad009]
  Placement = pos=(0,0,0) rot=(1,0,0;1.5708rad)
FEATURE [Sketcher::SketchObject] Sketch020  label="Side mounting holes spec"
  ExternalGeometry = -> [Mirrored004]
  FullyConstrained = false
  MapMode = 5
  Placement = pos=(59.85,-1.32e-14,1.32e-14) rot=(0.707107,0,0.707107;3.14159rad)
  Support = -> [Mirrored004]
  sketch-geometry (6):
    g0: Circle CenterX=16 CenterY=-7 CenterZ=0 NormalX=0 NormalY=0 NormalZ=1 AngleXU=0 Radius=2.25
    g1: Circle CenterX=52 CenterY=-7 CenterZ=0 NormalX=0 NormalY=0 NormalZ=1 AngleXU=0 Radius=2.25
    g2: LineSegment StartX=52 StartY=-7 StartZ=0 EndX=52 EndY=-13.5 EndZ=0
    g3: LineSegment StartX=52 StartY=-7 StartZ=0 EndX=58 EndY=-7 EndZ=0
    g4: LineSegment StartX=52 StartY=-7 StartZ=0 EndX=16 EndY=-7 EndZ=0
    g5: LineSegment StartX=16 StartY=-7 StartZ=0 EndX=16 EndY=-13.5 EndZ=0
  constraints (15):
    c: Coincident(g2,g1)
    c: Coincident(g2,g3)
    c: Horizontal(g3)
    c: PointOnObject(g2,g-5)
    c: Symmetric(g-6,g-5,g2)
    c: PointOnObject(g3,g-6)
    c: DistanceY(g3,g-6) = 7
    c: Coincident(g4,g1)
    c: Coincident(g4,g0)
    c: Horizontal(g4)
    c: Coincident(g5,g0)
    c: Perpendicular(g5,g-3) = 4.71239
    c: Symmetric(g-3,g-4,g5)
    c: Radius(g0) = 2.25
    c: Equal(g0,g1)
FEATURE [PartDesign::Pocket] Pocket009  label="Add side mounting holes"
  AllowMultiFace = false
  BaseFeature = -> Mirrored004
  Direction = (1,1,1)
  Length = 5
  Length2 = 100
  Placement = pos=(0,0,0) rot=(1,0,0;1.5708rad)
  Profile = -> Sketch020
  Type = 1
FEATURE [Sketcher::SketchObject] Sketch021  label="Side mounting holes nut trap spec"
  ExternalGeometry = -> [Pocket009]
  FullyConstrained = false
  MapMode = 5
  Placement = pos=(-53.85,0,0) rot=(0.707107,0,0.707107;3.14159rad)
  Support = -> [Pocket009]
  sketch-geometry (14):
    g0: LineSegment StartX=19.5 StartY=-9.02073 StartZ=0 EndX=19.5 EndY=-4.97927 EndZ=0
    g1: LineSegment StartX=19.5 StartY=-4.97927 StartZ=0 EndX=16 EndY=-2.95855 EndZ=0
    g2: LineSegment StartX=16 StartY=-2.95855 StartZ=0 EndX=12.5 EndY=-4.97927 EndZ=0
    g3: LineSegment StartX=12.5 StartY=-4.97927 StartZ=0 EndX=12.5 EndY=-9.02073 EndZ=0
    g4: LineSegment StartX=12.5 StartY=-9.02073 StartZ=0 EndX=16 EndY=-11.0415 EndZ=0
    g5: LineSegment StartX=16 StartY=-11.0415 StartZ=0 EndX=19.5 EndY=-9.02073 EndZ=0
    g6: Circle CenterX=16 CenterY=-7 CenterZ=0 NormalX=0 NormalY=0 NormalZ=1 AngleXU=0 Radius=4.04145
    g7: LineSegment StartX=55.5 StartY=-9.02073 StartZ=0 EndX=55.5 EndY=-4.97927 EndZ=0
    g8: LineSegment StartX=55.5 StartY=-4.97927 StartZ=0 EndX=52 EndY=-2.95855 EndZ=0
    g9: LineSegment StartX=52 StartY=-2.95855 StartZ=0 EndX=48.5 EndY=-4.97927 EndZ=0
    g10: LineSegment StartX=48.5 StartY=-4.97927 StartZ=0 EndX=48.5 EndY=-9.02073 EndZ=0
    g11: LineSegment StartX=48.5 StartY=-9.02073 StartZ=0 EndX=52 EndY=-11.0415 EndZ=0
    g12: LineSegment StartX=52 StartY=-11.0415 StartZ=0 EndX=55.5 EndY=-9.02073 EndZ=0
    g13: Circle CenterX=52 CenterY=-7 CenterZ=0 NormalX=0 NormalY=0 NormalZ=1 AngleXU=0 Radius=4.04145
  constraints (32):
    c: Coincident(g0,g1)
    c: Coincident(g1,g2)
    c: Coincident(g2,g3)
    c: Coincident(g3,g4)
    c: Coincident(g4,g5)
    c: Coincident(g5,g0)
    c: Equal(g0, g1-g5) x5
    c: PointOnObject(g0,g6)
    c: PointOnObject(g1,g6)
    c: PointOnObject(g2,g6)
    c: PointOnObject(g3,g6)
    c: PointOnObject(g4,g6)
    c: PointOnObject(g5,g6)
    c: Coincident(g7,g8)
    c: Coincident(g8,g9)
    c: Coincident(g9,g10)
    c: Coincident(g10,g11)
    c: Coincident(g11,g12)
    c: Coincident(g12,g7)
    c: Equal(g7, g8-g12) x5
    c: PointOnObject(g7,g13)
    c: PointOnObject(g8,g13)
    c: PointOnObject(g9,g13)
    c: PointOnObject(g10,g13)
    c: PointOnObject(g11,g13)
    c: PointOnObject(g12,g13)
    c: Vertical(g0)
    c: Vertical(g7)
    c: Coincident(g6,g-3)
    c: Coincident(g13,g-4)
    c: Distance(g2,g0) = 7
    c: Equal(g13,g6)
FEATURE [PartDesign::Pocket] Pocket010  label="Add side mounting nut-traps"
  AllowMultiFace = false
  BaseFeature = -> Pocket009
  Direction = (1,1,1)
  Length = 3.5
  Length2 = 100
  Placement = pos=(0,0,0) rot=(1,0,0;1.5708rad)
  Profile = -> Sketch021
  Type = 0
FEATURE [Sketcher::SketchObject] Sketch022  label="Barrel-jack cutout spec"
  FullyConstrained = false
  MapMode = 5
  Placement = pos=(0,-3,-7e-16) rot=(1,0,0;1.5708rad)
  Support = -> [Pocket010]
  sketch-geometry (5):
    g0: LineSegment StartX=10.75 StartY=24.5 StartZ=0 EndX=21.25 EndY=24.5 EndZ=0
    g1: LineSegment StartX=21.25 StartY=24.5 StartZ=0 EndX=21.25 EndY=12 EndZ=0
    g2: LineSegment StartX=21.25 StartY=12 StartZ=0 EndX=10.75 EndY=12 EndZ=0
    g3: LineSegment StartX=10.75 StartY=12 StartZ=0 EndX=10.75 EndY=24.5 EndZ=0
    g4: LineSegment StartX=16 StartY=24.5 StartZ=0 EndX=16 EndY=12 EndZ=0
  constraints (14):
    c: Coincident(g0,g1)
    c: Coincident(g1,g2)
    c: Coincident(g2,g3)
    c: Coincident(g3,g0)
    c: Horizontal(g0)
    c: Vertical(g1)
    c: Vertical(g3)
    c: Distance(g0) = 10.5
    c: Distance(g3) = 12.5
    c: DistanceY(g1) = 12
    c: Perpendicular(g4,g2) = 4.71239
    c: Perpendicular(g4,g0) = 1.5708
    c: Symmetric(g0,g0,g4)
    c: DistanceX(g4) = 16
FEATURE [PartDesign::Pocket] Pocket011  label="Add barrel-jack cutout"
  AllowMultiFace = false
  BaseFeature = -> Pocket010
  Direction = (1,1,1)
  Length = 5
  Length2 = 100
  Placement = pos=(0,0,0) rot=(1,0,0;1.5708rad)
  Profile = -> Sketch022
  Type = 1
FEATURE [PartDesign::Chamfer] Chamfer002
  Angle = 45
  Base = -> Pocket011 [Face5]
  BaseFeature = -> Pocket011
  ChamferType = 0
  FlipDirection = false
  Placement = pos=(0,0,0) rot=(1,0,0;1.5708rad)
  Size = 1
  Size2 = 1
  SupportTransform = false
  UseAllEdges = false
FEATURE [Sketcher::SketchObject] Sketch023
  FullyConstrained = false
  MapMode = 5
  Placement = pos=(0,0,0) rot=(1,0,0;1.5708rad)
  Support = -> [XZ_Plane010]
  sketch-geometry (7):
    g0: LineSegment StartX=2.25 StartY=0 StartZ=0 EndX=2.25 EndY=2.5 EndZ=0
    g1: LineSegment StartX=2.25 StartY=2.5 StartZ=0 EndX=8.55796 EndY=2.5 EndZ=0
    g2: LineSegment StartX=8.55796 StartY=2.5 StartZ=0 EndX=8.55796 EndY=0 EndZ=0
    g3: LineSegment StartX=8.55796 StartY=0 StartZ=0 EndX=7.5 EndY=-6 EndZ=0
    g4: LineSegment StartX=7.5 StartY=-6 StartZ=0 EndX=4.25 EndY=-6 EndZ=0
    g5: LineSegment StartX=4.25 StartY=-6 StartZ=0 EndX=4.25 EndY=0 EndZ=0
    g6: LineSegment StartX=4.25 StartY=0 StartZ=0 EndX=2.25 EndY=0 EndZ=0
  constraints (21):
    c: Coincident(g0,g1)
    c: Coincident(g1,g2)
    c: Coincident(g2,g3)
    c: Coincident(g3,g4)
    c: Coincident(g4,g5)
    c: Coincident(g5,g6)
    c: Horizontal(g4)
    c: Horizontal(g1)
    c: Horizontal(g6)
    c: Coincident(g0,g6)
    c: Vertical(g0)
    c: DistanceX(g0) = 2.25
    c: PointOnObject(g0,g-1)
    c: Vertical(g5)
    c: Vertical(g2)
    c: Distance(g0) = 2.5
    c: Distance(g2) = 2.5
    c: DistanceX(g5) = 4.25
    c: Distance(g5) = 6
    c: Distance(g4) = 3.25
    c: Angle(g3,g4) = 1.74533
FEATURE [PartDesign::Revolution] Revolution001
  AllowMultiFace = false
  Angle = 360
  Axis = (0,2e-16,1)
  Base = (0,0,0)
  Placement = pos=(0,0,0) rot=(1,0,0;1.5708rad)
  Profile = -> Sketch023
  ReferenceAxis = -> Sketch023 [V_Axis]
  Reversed = true
FEATURE [PartDesign::Fillet] Fillet002
  Base = -> Revolution001 [Face5]
  BaseFeature = -> Revolution001
  Placement = pos=(0,0,0) rot=(1,0,0;1.5708rad)
  Radius = 0.5
  SupportTransform = false
  UseAllEdges = false
FEATURE [PartDesign::Chamfer] Chamfer003
  Angle = 45
  Base = -> Fillet002 [Face5]
  BaseFeature = -> Fillet002
  ChamferType = 0
  FlipDirection = false
  Placement = pos=(0,0,0) rot=(1,0,0;1.5708rad)
  Size = 0.4
  Size2 = 1
  SupportTransform = false
  UseAllEdges = false
FEATURE [PartDesign::Body] Body006  label="Foot001"
  Group = -> [Sketch023,Revolution001,Fillet002,Chamfer003]
  Origin = -> Origin010
  Placement = pos=(-49,-53,0.5) rot=(0,0,1;0rad)
  Tip = -> Chamfer003
FEATURE [Part::FeaturePython] Array004  label="Foot array"  # Draft array (typed FeaturePython)
  Angle = 360
  ArrayType = 0
  Axis = (0,0,1)
  Base = -> Body006
  Center = (0,0,0)
  Fuse = false
  IntervalAxis = (0,0,0)
  IntervalX = (98,0,0)
  IntervalY = (0,106,0)
  IntervalZ = (0,0,1)
  NumberPolar = 1
  NumberX = 2
  NumberY = 2
  NumberZ = 1
  Placement = pos=(0,0,-3) rot=(0,0,1;0rad)
FEATURE [PartDesign::Chamfer] Chamfer004
  Angle = 45
  Base = -> Pocket005 [Face5]
  BaseFeature = -> Pocket005
  ChamferType = 0
  FlipDirection = false
  Placement = pos=(0,0,0) rot=(1,0,0;1.5708rad)
  Size = 1
  Size2 = 1
  SupportTransform = false
  UseAllEdges = false
FEATURE [PartDesign::Chamfer] Chamfer005
  Angle = 45
  Base = -> Chamfer004 [Edge1,Edge4]
  BaseFeature = -> Chamfer004
  ChamferType = 0
  FlipDirection = false
  Placement = pos=(0,0,0) rot=(1,0,0;1.5708rad)
  Size = 1
  Size2 = 1
  SupportTransform = false
  UseAllEdges = false
FEATURE [PartDesign::Chamfer] Chamfer006
  Angle = 45
  Base = -> Chamfer001 [Edge8]
  BaseFeature = -> Chamfer001
  ChamferType = 0
  FlipDirection = false
  Placement = pos=(0,0,0) rot=(1,0,0;1.5708rad)
  Size = 1
  Size2 = 1
  SupportTransform = false
  UseAllEdges = false
FEATURE [PartDesign::Chamfer] Chamfer007
  Angle = 45
  Base = -> Chamfer002 [Edge1,Edge4]
  BaseFeature = -> Chamfer002
  ChamferType = 0
  FlipDirection = false
  Placement = pos=(0,0,0) rot=(1,0,0;1.5708rad)
  Size = 1
  Size2 = 1
  SupportTransform = false
  UseAllEdges = false
FEATURE [PartDesign::Chamfer] Chamfer008
  Angle = 45
  Base = -> Chamfer005 [Edge43,Edge42]
  BaseFeature = -> Chamfer005
  ChamferType = 0
  FlipDirection = false
  Placement = pos=(0,0,0) rot=(1,0,0;1.5708rad)
  Size = 1
  Size2 = 1
  SupportTransform = false
  UseAllEdges = false
FEATURE [PartDesign::Chamfer] Chamfer009
  Angle = 45
  Base = -> Chamfer007 [Edge50,Edge51]
  BaseFeature = -> Chamfer007
  ChamferType = 0
  FlipDirection = false
  Placement = pos=(0,0,0) rot=(1,0,0;1.5708rad)
  Size = 1
  Size2 = 1
  SupportTransform = false
  UseAllEdges = false
FEATURE [PartDesign::Mirrored] Mirrored005  label="Add other side mounting nut traps"
  BaseFeature = -> Chamfer008
  MirrorPlane = -> YZ_Plane008
  Originals = -> [Pocket005]
  Placement = pos=(0,0,0) rot=(1,0,0;1.5708rad)
FEATURE [Sketcher::SketchObject] Sketch024  label="Switchgear holes spec"
  ExternalGeometry = -> [Mirrored005]
  FullyConstrained = true
  MapMode = 5
  Placement = pos=(0,-3,-7e-16) rot=(1,0,0;1.5708rad)
  Support = -> [Mirrored005]
  sketch-geometry (13):
    g0: LineSegment StartX=-40.725 StartY=43.625 StartZ=0 EndX=-33.675 EndY=43.625 EndZ=0
    g1: LineSegment StartX=-33.675 StartY=43.625 StartZ=0 EndX=-33.675 EndY=24.375 EndZ=0
    g2: LineSegment StartX=-33.675 StartY=24.375 StartZ=0 EndX=-40.725 EndY=24.375 EndZ=0
    g3: LineSegment StartX=-40.725 StartY=24.375 StartZ=0 EndX=-40.725 EndY=43.625 EndZ=0
    g4: LineSegment StartX=-40.725 StartY=43.625 StartZ=0 EndX=-33.675 EndY=24.375 EndZ=0
    g5: LineSegment StartX=-33.675 StartY=43.625 StartZ=0 EndX=-40.725 EndY=24.375 EndZ=0
    g6: GeomPoint X=-37.2 Y=34 Z=0
    g7: Circle CenterX=-12.4 CenterY=34 CenterZ=0 NormalX=0 NormalY=0 NormalZ=1 AngleXU=0 Radius=2.64
    g8: Circle CenterX=37.2 CenterY=34 CenterZ=0 NormalX=0 NormalY=0 NormalZ=1 AngleXU=0 Radius=8.15
    g9: LineSegment StartX=-37.2 StartY=34 StartZ=0 EndX=-12.4 EndY=34 EndZ=0
    g10: LineSegment StartX=-12.4 StartY=34 StartZ=0 EndX=12.4 EndY=34 EndZ=0
    g11: LineSegment StartX=12.4 StartY=34 StartZ=0 EndX=37.2 EndY=34 EndZ=0
    g12: LineSegment StartX=-37.2 StartY=34 StartZ=0 EndX=-62 EndY=34 EndZ=0
  constraints (32):
    c: Coincident(g0,g1)
    c: Coincident(g1,g2)
    c: Coincident(g2,g3)
    c: Coincident(g3,g0)
    c: Horizontal(g0)
    c: Horizontal(g2)
    c: Vertical(g1)
    c: Vertical(g3)
    c: Distance(g1) = 19.25
    c: Distance(g0) = 7.05
    c: Coincident(g4,g0)
    c: Coincident(g5,g0)
    c: Coincident(g4,g1)
    c: Coincident(g5,g2)
    c: PointOnObject(g6,g4)
    c: PointOnObject(g6,g5)
    c: Radius(g7) = 2.64
    c: Coincident(g7,g9)
    c: Coincident(g9,g6)
    c: Horizontal(g9)
    c: Equal(g11,g10)
    c: Equal(g10,g9)
    c: Horizontal(g10)
    c: Coincident(g10,g11)
    c: Coincident(g10,g7)
    c: Coincident(g11,g8)
    c: Coincident(g6,g12)
    c: Perpendicular(g12,g-3) = 4.71239
    c: Symmetric(g6,g8,g-2)
    c: Equal(g12,g9)
    c: Symmetric(g-3,g-3,g12)
    c: Radius(g8) = 8.15
FEATURE [PartDesign::Pocket] Pocket012  label="Add switchgear holes"
  AllowMultiFace = false
  BaseFeature = -> Mirrored005
  Direction = (1,1,1)
  Length = 5
  Length2 = 100
  Placement = pos=(0,0,0) rot=(1,0,0;1.5708rad)
  Profile = -> Sketch024
  Type = 1
FEATURE [Sketcher::SketchObject] Sketch025  label="Switch backface thinning tool"
  ExternalGeometry = -> [Pocket012]
  FullyConstrained = true
  MapMode = 5
  Placement = pos=(0,-1e-16,0) rot=(-1,0,0;1.5708rad)
  Support = -> [Pocket012]
  sketch-geometry (6):
    g0: LineSegment StartX=-40.725 StartY=-20.375 StartZ=0 EndX=-33.675 EndY=-20.375 EndZ=0
    g1: LineSegment StartX=-33.675 StartY=-20.375 StartZ=0 EndX=-33.675 EndY=-43.625 EndZ=0
    g2: LineSegment StartX=-33.675 StartY=-47.625 StartZ=0 EndX=-40.725 EndY=-47.625 EndZ=0
    g3: LineSegment StartX=-40.725 StartY=-47.625 StartZ=0 EndX=-40.725 EndY=-24.375 EndZ=0
    g4: LineSegment StartX=-33.675 StartY=-43.625 StartZ=0 EndX=-33.675 EndY=-47.625 EndZ=0
    g5: LineSegment StartX=-40.725 StartY=-24.375 StartZ=0 EndX=-40.725 EndY=-20.375 EndZ=0
  constraints (16):
    c: Coincident(g0,g1)
    c: Coincident(g2,g3)
    c: Horizontal(g0)
    c: Horizontal(g2)
    c: Vertical(g1)
    c: Vertical(g3)
    c: Coincident(g1,g4)
    c: Coincident(g1,g-4)
    c: Coincident(g4,g2)
    c: Vertical(g4)
    c: Coincident(g3,g-3)
    c: Coincident(g3,g5)
    c: Coincident(g5,g0)
    c: Vertical(g5)
    c: Equal(g5,g4)
    c: Distance(g5) = 4
FEATURE [PartDesign::Pocket] Pocket013  label="Thin backwall for switch to 2mm"
  AllowMultiFace = false
  BaseFeature = -> Pocket012
  Direction = (1,1,1)
  Length = 1
  Length2 = 100
  Placement = pos=(0,0,0) rot=(1,0,0;1.5708rad)
  Profile = -> Sketch025
  Type = 0
FEATURE [PartDesign::Mirrored] Mirrored006  label="Add other side nut traps"
  BaseFeature = -> Chamfer009
  MirrorPlane = -> YZ_Plane009
  Originals = -> [Pocket010]
  Placement = pos=(0,0,0) rot=(1,0,0;1.5708rad)
FEATURE [PartDesign::Chamfer] Chamfer010  label="Make LED hole pretty chamfer"
  Angle = 45
  Base = -> Pocket013 [Edge101]
  BaseFeature = -> Pocket013
  ChamferType = 0
  FlipDirection = false
  Placement = pos=(0,0,0) rot=(1,0,0;1.5708rad)
  Size = 2
  Size2 = 1
  SupportTransform = false
  UseAllEdges = false
FEATURE [Sketcher::SketchObject] Sketch026  label="Decorative feature for LED hole"
  ExternalGeometry = -> [Chamfer010]
  FullyConstrained = true
  MapMode = 5
  Placement = pos=(0,-3,-7e-16) rot=(1,0,0;1.5708rad)
  Support = -> [Chamfer010]
  sketch-geometry (4):
    g0: Circle CenterX=-12.4 CenterY=34 CenterZ=0 NormalX=0 NormalY=0 NormalZ=1 AngleXU=0 Radius=6.64
    g1: Circle CenterX=-12.4 CenterY=34 CenterZ=0 NormalX=0 NormalY=0 NormalZ=1 AngleXU=0 Radius=8.39
    g2: LineSegment StartX=-12.4 StartY=38.64 StartZ=0 EndX=-12.4 EndY=40.64 EndZ=0
    g3: LineSegment StartX=-5.76 StartY=34 StartZ=0 EndX=-4.01 EndY=34 EndZ=0
  constraints (10):
    c: Coincident(g0,g1)
    c: Coincident(g0,g-3)
    c: Perpendicular(g2,g-3) = 1.5708
    c: PointOnObject(g2,g0)
    c: Distance(g2) = 2
    c: Vertical(g2)
    c: Horizontal(g3)
    c: Perpendicular(g3,g0) = 1.5708
    c: PointOnObject(g3,g1)
    c: Distance(g3) = 1.75
FEATURE [PartDesign::Pocket] Pocket014  label="Add decorative feature for LED hole"
  AllowMultiFace = false
  BaseFeature = -> Chamfer010
  Direction = (1,1,1)
  Length = 1.5
  Length2 = 100
  Placement = pos=(0,0,0) rot=(1,0,0;1.5708rad)
  Profile = -> Sketch026
  Type = 0
FEATURE [PartDesign::Chamfer] Chamfer011  label="Decorative feature easing chamfer"
  Angle = 45
  Base = -> Pocket014 [Edge39,Edge200]
  BaseFeature = -> Pocket014
  ChamferType = 0
  FlipDirection = false
  Placement = pos=(0,0,0) rot=(1,0,0;1.5708rad)
  Size = 0.35
  Size2 = 1
  SupportTransform = false
  UseAllEdges = false
FEATURE [PartDesign::Chamfer] Chamfer012  label="Switchgear easing-in chamfers"
  Angle = 45
  Base = -> Chamfer011 [Edge206,Edge184,Edge188,Edge205,Edge128]
  BaseFeature = -> Chamfer011
  ChamferType = 0
  FlipDirection = false
  Placement = pos=(0,0,0) rot=(1,0,0;1.5708rad)
  Size = 0.3
  Size2 = 1
  SupportTransform = false
  UseAllEdges = false
FEATURE [Sketcher::SketchObject] Sketch027  label="Joining Bar spec"
  FullyConstrained = false
  MapMode = 5
  Placement = pos=(0,0,0) rot=(0.57735,0.57735,0.57735;2.0944rad)
  Support = -> [YZ_Plane011]
  sketch-geometry (20):
    g0: LineSegment StartX=-37.25 StartY=83.9 StartZ=0 EndX=-37.25 EndY=72.1 EndZ=0
    g1: LineSegment StartX=-37.25 StartY=72.1 StartZ=0 EndX=37.25 EndY=72.1 EndZ=0
    g2: LineSegment StartX=37.25 StartY=72.1 StartZ=0 EndX=37.25 EndY=83.9 EndZ=0
    g3: LineSegment StartX=37.25 StartY=83.9 StartZ=0 EndX=52.75 EndY=83.9 EndZ=0
    g4: LineSegment StartX=52.75 StartY=83.9 StartZ=0 EndX=52.75 EndY=52.3 EndZ=0
    g5: LineSegment StartX=52.75 StartY=52.3 StartZ=0 EndX=37.25 EndY=52.3 EndZ=0
    g6: LineSegment StartX=37.25 StartY=52.3 StartZ=0 EndX=37.25 EndY=64.1 EndZ=0
    g7: LineSegment StartX=37.25 StartY=64.1 StartZ=0 EndX=-37.25 EndY=64.1 EndZ=0
    g8: LineSegment StartX=-37.25 StartY=64.1 StartZ=0 EndX=-37.25 EndY=52.3 EndZ=0
    g9: LineSegment StartX=-37.25 StartY=52.3 StartZ=0 EndX=-52.75 EndY=52.3 EndZ=0
    g10: LineSegment StartX=-52.75 StartY=52.3 StartZ=0 EndX=-52.75 EndY=83.9 EndZ=0
    g11: LineSegment StartX=-52.75 StartY=83.9 StartZ=0 EndX=-37.25 EndY=83.9 EndZ=0
    g12: Circle CenterX=45 CenterY=60.05 CenterZ=0 NormalX=0 NormalY=0 NormalZ=1 AngleXU=0 Radius=2.25
    g13: Circle CenterX=45 CenterY=76.15 CenterZ=0 NormalX=0 NormalY=0 NormalZ=1 AngleXU=0 Radius=2.25
    g14: LineSegment StartX=45 StartY=57.8 StartZ=0 EndX=45 EndY=52.3 EndZ=0
    g15: LineSegment StartX=42.75 StartY=60.05 StartZ=0 EndX=37.25 EndY=60.05 EndZ=0
    g16: LineSegment StartX=47.25 StartY=60.05 StartZ=0 EndX=52.75 EndY=60.05 EndZ=0
    g17: Circle CenterX=-45 CenterY=76.15 CenterZ=0 NormalX=0 NormalY=0 NormalZ=1 AngleXU=0 Radius=2.25
    g18: Circle CenterX=-45 CenterY=60.05 CenterZ=0 NormalX=0 NormalY=0 NormalZ=1 AngleXU=0 Radius=2.25
    g19: LineSegment StartX=52.75 StartY=68.1 StartZ=0 EndX=-52.75 EndY=68.1 EndZ=0
  constraints (52):
    c: Coincident(g0,g1)
    c: Coincident(g1,g2)
    c: Coincident(g2,g3)
    c: Coincident(g3,g4)
    c: Coincident(g4,g5)
    c: Coincident(g5,g6)
    c: Coincident(g6,g7)
    c: Coincident(g7,g8)
    c: Coincident(g8,g9)
    c: Coincident(g9,g10)
    c: Coincident(g10,g11)
    c: Coincident(g11,g0)
    c: Horizontal(g11)
    c: Horizontal(g9)
    c: Horizontal(g7)
    c: Horizontal(g3)
    c: Horizontal(g5)
    c: Vertical(g10)
    c: Vertical(g0)
    c: Vertical(g8)
    c: Vertical(g2)
    c: Vertical(g6)
    c: Equal(g3,g5)
    c: Equal(g5,g9)
    c: Equal(g9,g11)
    c: Equal(g0,g8)
    c: Equal(g8,g2)
    c: Equal(g2,g6)
    c: Symmetric(g1,g0,g-2)
    c: Distance(g0,g7) = 8
    c: Distance(g13,g12) = 16.1
    c: Perpendicular(g16,g12) = 1.5708
    c: Perpendicular(g15,g12) = 1.5708
    c: Perpendicular(g16,g4) = 4.71239
    c: Perpendicular(g15,g6) = 4.71239
    c: Perpendicular(g14,g12) = 1.5708
    c: Perpendicular(g14,g5) = 4.71239
    c: Radius(g17) = 2.25
    c: Equal(g17,g18)
    c: Equal(g17,g13)
    c: Equal(g17,g12)
    c: Perpendicular(g19,g10) = 4.71239
    c: Perpendicular(g19,g4) = 1.5708
    c: Symmetric(g9,g10,g19)
    c: Symmetric(g17,g18,g19)
    c: Symmetric(g13,g12,g19)
    c: Equal(g15,g16)
    c: Equal(g15,g14)
    c: Symmetric(g18,g12,g-2)
    c: Distance(g15) = 5.5
    c: Distance(g17,g13) = 90
    c: DistanceY(g19) = 68.1
FEATURE [PartDesign::Pad] Pad010  label="Make Joining bar"
  AllowMultiFace = false
  Direction = (1,1,1)
  Length = 3.5
  Length2 = 100
  Placement = pos=(0,0,0) rot=(0.57735,0.57735,0.57735;2.0944rad)
  Profile = -> Sketch027
  Type = 0
FEATURE [Sketcher::SketchObject] Sketch028  label="Nut trap outer walls"
  ExternalGeometry = -> [Pad010]
  FullyConstrained = false
  MapMode = 5
  Placement = pos=(-1e-16,0,0) rot=(0.57735,0.57735,-0.57735;4.18879rad)
  Support = -> [Pad010]
  sketch-geometry (16):
    g0: LineSegment StartX=48.7528 StartY=-66.55 StartZ=0 EndX=52.5056 EndY=-60.05 EndZ=0
    g1: LineSegment StartX=52.5056 StartY=-60.05 StartZ=0 EndX=48.7528 EndY=-53.55 EndZ=0
    g2: LineSegment StartX=48.7528 StartY=-53.55 StartZ=0 EndX=41.2472 EndY=-53.55 EndZ=0
    g3: LineSegment StartX=41.2472 StartY=-53.55 StartZ=0 EndX=37.4944 EndY=-60.05 EndZ=0
    g4: LineSegment StartX=37.4944 StartY=-60.05 StartZ=0 EndX=41.2472 EndY=-66.55 EndZ=0
    g5: LineSegment StartX=41.2472 StartY=-66.55 StartZ=0 EndX=48.7528 EndY=-66.55 EndZ=0
    g6: Circle CenterX=45 CenterY=-60.05 CenterZ=0 NormalX=0 NormalY=0 NormalZ=1 AngleXU=0 Radius=7.50555
    g7: LineSegment StartX=48.7528 StartY=-82.65 StartZ=0 EndX=52.5056 EndY=-76.15 EndZ=0
    g8: LineSegment StartX=52.5056 StartY=-76.15 StartZ=0 EndX=48.7528 EndY=-69.65 EndZ=0
    g9: LineSegment StartX=48.7528 StartY=-69.65 StartZ=0 EndX=41.2472 EndY=-69.65 EndZ=0
    g10: LineSegment StartX=41.2472 StartY=-69.65 StartZ=0 EndX=37.4944 EndY=-76.15 EndZ=0
    g11: LineSegment StartX=37.4944 StartY=-76.15 StartZ=0 EndX=41.2472 EndY=-82.65 EndZ=0
    g12: LineSegment StartX=41.2472 StartY=-82.65 StartZ=0 EndX=48.7528 EndY=-82.65 EndZ=0
    g13: Circle CenterX=45 CenterY=-76.15 CenterZ=0 NormalX=0 NormalY=0 NormalZ=1 AngleXU=0 Radius=7.50555
    g14: Circle CenterX=45 CenterY=-60.05 CenterZ=0 NormalX=0 NormalY=0 NormalZ=1 AngleXU=0 Radius=2.25
    g15: Circle CenterX=45 CenterY=-76.15 CenterZ=0 NormalX=0 NormalY=0 NormalZ=1 AngleXU=0 Radius=2.25
  constraints (36):
    c: Coincident(g0,g1)
    c: Coincident(g1,g2)
    c: Coincident(g2,g3)
    c: Coincident(g3,g4)
    c: Coincident(g4,g5)
    c: Coincident(g5,g0)
    c: Equal(g0, g1-g5) x5
    c: PointOnObject(g0,g6)
    c: PointOnObject(g1,g6)
    c: PointOnObject(g2,g6)
    c: PointOnObject(g3,g6)
    c: PointOnObject(g4,g6)
    c: PointOnObject(g5,g6)
    c: Horizontal(g2)
    c: Coincident(g7,g8)
    c: Coincident(g8,g9)
    c: Coincident(g9,g10)
    c: Coincident(g10,g11)
    c: Coincident(g11,g12)
    c: Coincident(g12,g7)
    c: Equal(g7, g8-g12) x5
    c: PointOnObject(g7,g13)
    c: PointOnObject(g8,g13)
    c: PointOnObject(g9,g13)
    c: PointOnObject(g10,g13)
    c: PointOnObject(g11,g13)
    c: PointOnObject(g12,g13)
    c: Horizontal(g9)
    c: Equal(g13,g6)
    c: Distance(g2,g4) = 13
    c: Coincident(g6,g-4)
    c: Coincident(g13,g-3)
    c: Coincident(g15,g13)
    c: Coincident(g14,g6)
    c: Equal(g14,g15)
    c: Equal(g15,g-3)
FEATURE [PartDesign::Pad] Pad011  label="Add nut trap outer walls"
  AllowMultiFace = false
  BaseFeature = -> Pad010
  Direction = (1,1,1)
  Length = 2.5
  Length2 = 100
  Placement = pos=(0,0,0) rot=(0.57735,0.57735,0.57735;2.0944rad)
  Profile = -> Sketch028
  Type = 0
FEATURE [PartDesign::Mirrored] Mirrored007  label="Add mirror of nut trap outer walls"
  BaseFeature = -> Pad011
  MirrorPlane = -> Sketch028 [V_Axis]
  Originals = -> [Pad011]
  Placement = pos=(0,0,0) rot=(0.57735,0.57735,0.57735;2.0944rad)
FEATURE [Sketcher::SketchObject] Sketch029  label="Nut trap spec for bar"
  ExternalGeometry = -> [Mirrored007]
  FullyConstrained = false
  MapMode = 5
  Placement = pos=(-2.5,1.1e-15,-1.1e-15) rot=(0.57735,0.57735,-0.57735;4.18879rad)
  Support = -> [Mirrored007]
  sketch-geometry (14):
    g0: LineSegment StartX=-42.9793 StartY=-63.55 StartZ=0 EndX=-40.9585 EndY=-60.05 EndZ=0
    g1: LineSegment StartX=-40.9585 StartY=-60.05 StartZ=0 EndX=-42.9793 EndY=-56.55 EndZ=0
    g2: LineSegment StartX=-42.9793 StartY=-56.55 StartZ=0 EndX=-47.0207 EndY=-56.55 EndZ=0
    g3: LineSegment StartX=-47.0207 StartY=-56.55 StartZ=0 EndX=-49.0415 EndY=-60.05 EndZ=0
    g4: LineSegment StartX=-49.0415 StartY=-60.05 StartZ=0 EndX=-47.0207 EndY=-63.55 EndZ=0
    g5: LineSegment StartX=-47.0207 StartY=-63.55 StartZ=0 EndX=-42.9793 EndY=-63.55 EndZ=0
    g6: Circle CenterX=-45 CenterY=-60.05 CenterZ=0 NormalX=0 NormalY=0 NormalZ=1 AngleXU=0 Radius=4.04145
    g7: LineSegment StartX=-42.9793 StartY=-79.65 StartZ=0 EndX=-40.9585 EndY=-76.15 EndZ=0
    g8: LineSegment StartX=-40.9585 StartY=-76.15 StartZ=0 EndX=-42.9793 EndY=-72.65 EndZ=0
    g9: LineSegment StartX=-42.9793 StartY=-72.65 StartZ=0 EndX=-47.0207 EndY=-72.65 EndZ=0
    g10: LineSegment StartX=-47.0207 StartY=-72.65 StartZ=0 EndX=-49.0415 EndY=-76.15 EndZ=0
    g11: LineSegment StartX=-49.0415 StartY=-76.15 StartZ=0 EndX=-47.0207 EndY=-79.65 EndZ=0
    g12: LineSegment StartX=-47.0207 StartY=-79.65 StartZ=0 EndX=-42.9793 EndY=-79.65 EndZ=0
    g13: Circle CenterX=-45 CenterY=-76.15 CenterZ=0 NormalX=0 NormalY=0 NormalZ=1 AngleXU=0 Radius=4.04145
  constraints (32):
    c: Coincident(g0,g1)
    c: Coincident(g1,g2)
    c: Coincident(g2,g3)
    c: Coincident(g3,g4)
    c: Coincident(g4,g5)
    c: Coincident(g5,g0)
    c: Equal(g0, g1-g5) x5
    c: PointOnObject(g0,g6)
    c: PointOnObject(g1,g6)
    c: PointOnObject(g2,g6)
    c: PointOnObject(g3,g6)
    c: PointOnObject(g4,g6)
    c: PointOnObject(g5,g6)
    c: Coincident(g7,g8)
    c: Coincident(g8,g9)
    c: Coincident(g9,g10)
    c: Coincident(g10,g11)
    c: Coincident(g11,g12)
    c: Coincident(g12,g7)
    c: Equal(g7, g8-g12) x5
    c: PointOnObject(g7,g13)
    c: PointOnObject(g8,g13)
    c: PointOnObject(g9,g13)
    c: PointOnObject(g10,g13)
    c: PointOnObject(g11,g13)
    c: PointOnObject(g12,g13)
    c: Horizontal(g5)
    c: Horizontal(g9)
    c: Coincident(g6,g-3)
    c: Coincident(g13,g-4)
    c: Equal(g6,g13)
    c: Distance(g0,g1) = 7
FEATURE [PartDesign::Pocket] Pocket015  label="Add nut traps for bar"
  AllowMultiFace = false
  BaseFeature = -> Mirrored007
  Direction = (1,1,1)
  Length = 4
  Length2 = 100
  Placement = pos=(0,0,0) rot=(0.57735,0.57735,0.57735;2.0944rad)
  Profile = -> Sketch029
  Type = 0
FEATURE [PartDesign::Mirrored] Mirrored008  label="Add other nut traps for bar"
  BaseFeature = -> Pocket015
  MirrorPlane = -> XZ_Plane011
  Originals = -> [Pocket015]
  Placement = pos=(0,0,0) rot=(0.57735,0.57735,0.57735;2.0944rad)
FEATURE [PartDesign::Fillet] Fillet003  label="Round corners off and Dogbone!"
  Base = -> Mirrored008 [Edge8,Edge58,Edge1,Edge2,Edge5,Edge60,Edge63,Edge64,Edge62,Edge59,Edge57,Edge61]
  BaseFeature = -> Mirrored008
  Placement = pos=(0,0,0) rot=(0.57735,0.57735,0.57735;2.0944rad)
  Radius = 4
  SupportTransform = false
  UseAllEdges = false
FEATURE [PartDesign::Chamfer] Chamfer013  label="Screw penetration aid chamfers"
  Angle = 45
  Base = -> Fillet003 [Face52,Face51,Face54,Face53]
  BaseFeature = -> Fillet003
  ChamferType = 0
  FlipDirection = false
  Placement = pos=(0,0,0) rot=(0.57735,0.57735,0.57735;2.0944rad)
  Size = 0.35
  Size2 = 1
  SupportTransform = false
  UseAllEdges = false
FEATURE [PartDesign::Chamfer] Chamfer014  label="Print and fitting aid chamfer"
  Angle = 45
  Base = -> Chamfer013 [Edge6]
  BaseFeature = -> Chamfer013
  ChamferType = 0
  FlipDirection = false
  Placement = pos=(0,0,0) rot=(0.57735,0.57735,0.57735;2.0944rad)
  Size = 0.5
  Size2 = 1
  SupportTransform = false
  UseAllEdges = false
FEATURE [PartDesign::Body] Body007  label="Joining bar"
  Group = -> [Sketch027,Pad010,Sketch028,Pad011,Mirrored007,Sketch029,Pocket015,Mirrored008,Fillet003,Chamfer013,Chamfer014]
  Origin = -> Origin011
  Placement = pos=(56,0,0) rot=(0,0,1;0rad)
  Tip = -> Chamfer014
FEATURE [Sketcher::SketchObject] Sketch030  label="LED guide tube spec"
  ExternalGeometry = -> [Chamfer012]
  FullyConstrained = true
  MapMode = 5
  Placement = pos=(0,-1e-16,0) rot=(-1,0,0;1.5708rad)
  Support = -> [Chamfer012]
  sketch-geometry (3):
    g0: Circle CenterX=-12.4 CenterY=-34 CenterZ=0 NormalX=0 NormalY=0 NormalZ=1 AngleXU=0 Radius=2.64
    g1: Circle CenterX=-12.4 CenterY=-34 CenterZ=0 NormalX=0 NormalY=0 NormalZ=1 AngleXU=0 Radius=5.14
    g2: LineSegment StartX=-9.76 StartY=-34 StartZ=0 EndX=-7.26 EndY=-34 EndZ=0
  constraints (7):
    c: Coincident(g0,g1)
    c: Coincident(g0,g-3)
    c: Equal(g0,g-3)
    c: Horizontal(g2)
    c: Perpendicular(g2,g0) = 1.5708
    c: PointOnObject(g2,g1)
    c: Distance(g2) = 2.5
FEATURE [PartDesign::Pad] Pad012  label="Add LED Guide Tube"
  AllowMultiFace = false
  BaseFeature = -> Chamfer012
  Direction = (1,1,1)
  Length = 4
  Length2 = 100
  Placement = pos=(0,0,0) rot=(1,0,0;1.5708rad)
  Profile = -> Sketch030
  Type = 0
FEATURE [Sketcher::SketchObject] Sketch031  label="LED Guide tube splitter tool"
  ExternalGeometry = -> [Pad012]
  FullyConstrained = true
  MapMode = 5
  Placement = pos=(0,4,-9e-16) rot=(-1,0,0;1.5708rad)
  Support = -> [Pad012]
  sketch-geometry (5):
    g0: LineSegment StartX=-17.54 StartY=-33 StartZ=0 EndX=-7.26 EndY=-33 EndZ=0
    g1: LineSegment StartX=-7.26 StartY=-33 StartZ=0 EndX=-7.26 EndY=-35 EndZ=0
    g2: LineSegment StartX=-7.26 StartY=-35 StartZ=0 EndX=-17.54 EndY=-35 EndZ=0
    g3: LineSegment StartX=-17.54 StartY=-35 StartZ=0 EndX=-17.54 EndY=-33 EndZ=0
    g4: LineSegment StartX=-17.54 StartY=-34 StartZ=0 EndX=-7.26 EndY=-34 EndZ=0
  constraints (14):
    c: Coincident(g0,g1)
    c: Coincident(g1,g2)
    c: Coincident(g2,g3)
    c: Coincident(g3,g0)
    c: Horizontal(g0)
    c: Horizontal(g2)
    c: Vertical(g1)
    c: Tangent(g1,g-3)
    c: Tangent(g3,g-3)
    c: Distance(g1) = 2
    c: Perpendicular(g4,g3) = 1.5708
    c: Perpendicular(g4,g1) = 4.71239
    c: Symmetric(g1,g0,g4)
    c: PointOnObject(g-3,g4)
FEATURE [PartDesign::Pocket] Pocket016  label="Split guide tube"
  AllowMultiFace = false
  BaseFeature = -> Pad012
  Direction = (1,1,1)
  Length = 0
  Length2 = 100
  Placement = pos=(0,0,0) rot=(1,0,0;1.5708rad)
  Profile = -> Sketch031
  Type = 3
  UpToFace = -> Pad012 [Face3]
FEATURE [PartDesign::Pocket] Pocket017  label="Add PCB Screwholes"
  AllowMultiFace = false
  BaseFeature = -> Pad005
  Direction = (1,1,1)
  Length = 5
  Length2 = 100
  Profile = -> Sketch010
  Type = 1
FEATURE [PartDesign::Chamfer] Chamfer015
  Angle = 45
  Base = -> Pocket017 [Edge6,Edge9]
  BaseFeature = -> Pocket017
  ChamferType = 0
  FlipDirection = false
  Size = 1
  Size2 = 1
  SupportTransform = false
  UseAllEdges = false
FEATURE [PartDesign::Body] Body001  label="Base plate"
  Group = -> [Sketch001,Pad,Sketch009,Pad005,Sketch010,Pocket017,Chamfer015]
  Origin = -> Origin005
  Tip = -> Chamfer015
FEATURE [Sketcher::SketchObject] Sketch032
  FullyConstrained = true
  MapMode = 5
  Placement = pos=(-60,0,0) rot=(0.707107,0,0.707107;3.14159rad)
  Support = -> [Chamfer006]
  sketch-geometry (4):
    g0: ArcOfCircle CenterX=55 CenterY=32.5 CenterZ=0 NormalX=0 NormalY=0 NormalZ=1 AngleXU=0 Radius=1.5 StartAngle=5.59e-14 EndAngle=3.14159
    g1: ArcOfCircle CenterX=55 CenterY=-32.5 CenterZ=0 NormalX=0 NormalY=0 NormalZ=1 AngleXU=0 Radius=1.5 StartAngle=3.14159 EndAngle=6.28319
    g2: LineSegment StartX=53.5 StartY=32.5 StartZ=0 EndX=53.5 EndY=-32.5 EndZ=0
    g3: LineSegment StartX=56.5 StartY=32.5 StartZ=0 EndX=56.5 EndY=-32.5 EndZ=0
  constraints (9):
    c: Tangent(g0,g3) = 1.5708
    c: Tangent(g0,g2) = -1.5708
    c: Tangent(g2,g1) = -1.5708
    c: Tangent(g3,g1) = 1.5708
    c: Vertical(g2)
    c: Distance(g1,g1) = 3
    c: DistanceX(g1) = 55
    c: Symmetric(g1,g0,g-1)
    c: Distance(g3) = 65
FEATURE [PartDesign::Pad] Pad013
  AllowMultiFace = false
  BaseFeature = -> Chamfer006
  Direction = (1,1,1)
  Length = 4
  Length2 = 100
  Placement = pos=(0,0,0) rot=(1,0,0;1.5708rad)
  Profile = -> Sketch032
  Type = 0
FEATURE [Sketcher::SketchObject] Sketch033  label="Hoop profile"
  FullyConstrained = false
  MapMode = 5
  Support = -> [XY_Plane012]
  sketch-geometry (3):
    g0: Circle CenterX=0 CenterY=0 CenterZ=0 NormalX=0 NormalY=0 NormalZ=1 AngleXU=0 Radius=6.75
    g1: Circle CenterX=0 CenterY=0 CenterZ=0 NormalX=0 NormalY=0 NormalZ=1 AngleXU=0 Radius=8.2
    g2: LineSegment StartX=-8.2 StartY=1.2e-15 StartZ=0 EndX=-6.75 EndY=1.2e-15 EndZ=0
  constraints (7):
    c: Coincident(g0,g-1)
    c: Radius(g0) = 6.75
    c: Coincident(g1,g0)
    c: Perpendicular(g2,g0) = 4.71239
    c: Horizontal(g2)
    c: Perpendicular(g2,g1) = 4.71239
    c: Distance(g2) = 1.45
FEATURE [PartDesign::Pad] Pad014  label="Make hoop"
  AllowMultiFace = false
  Direction = (1,1,1)
  Length = 1.75
  Length2 = 100
  Profile = -> Sketch033
  Type = 0
FEATURE [Sketcher::SketchObject] Sketch034  label="Panel stiffeners"
  FullyConstrained = false
  MapMode = 5
  Placement = pos=(0,-1e-16,0) rot=(-1,0,0;1.5708rad)
  Support = -> [Mirrored006]
  sketch-geometry (8):
    g0: ArcOfCircle CenterX=-22.5 CenterY=-6 CenterZ=0 NormalX=0 NormalY=0 NormalZ=1 AngleXU=0 Radius=1.5 StartAngle=1.5708 EndAngle=4.71239
    g1: ArcOfCircle CenterX=22.5 CenterY=-6 CenterZ=0 NormalX=0 NormalY=0 NormalZ=1 AngleXU=0 Radius=1.5 StartAngle=4.71239 EndAngle=7.85398
    g2: LineSegment StartX=-22.5 StartY=-7.5 StartZ=0 EndX=22.5 EndY=-7.5 EndZ=0
    g3: LineSegment StartX=-22.5 StartY=-4.5 StartZ=0 EndX=22.5 EndY=-4.5 EndZ=0
    g4: ArcOfCircle CenterX=-47.5 CenterY=-35 CenterZ=0 NormalX=0 NormalY=0 NormalZ=1 AngleXU=0 Radius=1.5 StartAngle=1.5708 EndAngle=4.71239
    g5: ArcOfCircle CenterX=47.5 CenterY=-35 CenterZ=0 NormalX=0 NormalY=0 NormalZ=1 AngleXU=0 Radius=1.5 StartAngle=4.71239 EndAngle=7.85398
    g6: LineSegment StartX=-47.5 StartY=-36.5 StartZ=0 EndX=47.5 EndY=-36.5 EndZ=0
    g7: LineSegment StartX=-47.5 StartY=-33.5 StartZ=0 EndX=47.5 EndY=-33.5 EndZ=0
  constraints (18):
    c: Tangent(g0,g3) = 1.5708
    c: Tangent(g0,g2) = -1.5708
    c: Tangent(g2,g1) = -1.5708
    c: Tangent(g3,g1) = 1.5708
    c: Horizontal(g2)
    c: Tangent(g4,g7) = 1.5708
    c: Tangent(g4,g6) = -1.5708
    c: Tangent(g6,g5) = -1.5708
    c: Tangent(g7,g5) = 1.5708
    c: Horizontal(g6)
    c: Symmetric(g4,g5,g-2)
    c: Distance(g4,g4) = 3
    c: Distance(g5,g4) = 95
    c: DistanceY(g4) = -35
    c: Symmetric(g0,g1,g-2)
    c: Distance(g1,g1) = 3
    c: Distance(g1,g0) = 45
    c: DistanceY(g0) = -6
FEATURE [PartDesign::Pad] Pad015  label="Add panel stiffeners"
  AllowMultiFace = false
  BaseFeature = -> Mirrored006
  Direction = (1,1,1)
  Length = 2
  Length2 = 100
  Placement = pos=(0,0,0) rot=(1,0,0;1.5708rad)
  Profile = -> Sketch034
  Type = 0
FEATURE [PartDesign::Body] Body005  label="Rear Endplate"
  Group = -> [Sketch018,Pad008,Sketch019,Pad009,Mirrored004,Sketch020,Pocket009,Sketch021,Pocket010,Sketch022,Pocket011,Chamfer002,Chamfer007,Chamfer009,Mirrored006,Sketch034,Pad015]
  Origin = -> Origin009
  Placement = pos=(0,66.95,0) rot=(0,0,1;3.14159rad)
  Tip = -> Pad015
FEATURE [Sketcher::SketchObject] Sketch035  label="Stiffening bars for front plate"
  FullyConstrained = true
  MapMode = 5
  Placement = pos=(0,-1e-16,0) rot=(-1,0,0;1.5708rad)
  Support = -> [Pocket016]
  sketch-geometry (8):
    g0: ArcOfCircle CenterX=-40 CenterY=-55 CenterZ=0 NormalX=0 NormalY=0 NormalZ=1 AngleXU=0 Radius=1.5 StartAngle=1.5708 EndAngle=4.71239
    g1: ArcOfCircle CenterX=40 CenterY=-55 CenterZ=0 NormalX=0 NormalY=0 NormalZ=1 AngleXU=0 Radius=1.5 StartAngle=4.71239 EndAngle=7.85398
    g2: LineSegment StartX=-40 StartY=-56.5 StartZ=0 EndX=40 EndY=-56.5 EndZ=0
    g3: LineSegment StartX=-40 StartY=-53.5 StartZ=0 EndX=40 EndY=-53.5 EndZ=0
    g4: ArcOfCircle CenterX=-40 CenterY=-12 CenterZ=0 NormalX=0 NormalY=0 NormalZ=1 AngleXU=0 Radius=1.5 StartAngle=1.5708 EndAngle=4.71239
    g5: ArcOfCircle CenterX=40 CenterY=-12 CenterZ=0 NormalX=0 NormalY=0 NormalZ=1 AngleXU=0 Radius=1.5 StartAngle=4.71239 EndAngle=7.85398
    g6: LineSegment StartX=-40 StartY=-13.5 StartZ=0 EndX=40 EndY=-13.5 EndZ=0
    g7: LineSegment StartX=-40 StartY=-10.5 StartZ=0 EndX=40 EndY=-10.5 EndZ=0
  constraints (18):
    c: Tangent(g0,g3) = 1.5708
    c: Tangent(g0,g2) = -1.5708
    c: Tangent(g2,g1) = -1.5708
    c: Tangent(g3,g1) = 1.5708
    c: Horizontal(g2)
    c: Tangent(g4,g7) = 1.5708
    c: Tangent(g4,g6) = -1.5708
    c: Tangent(g6,g5) = -1.5708
    c: Tangent(g7,g5) = 1.5708
    c: Horizontal(g6)
    c: Equal(g3,g6)
    c: Distance(g5,g5) = 3
    c: Equal(g1,g5)
    c: Symmetric(g0,g1,g-2)
    c: Symmetric(g5,g4,g-2)
    c: DistanceY(g5) = -12
    c: DistanceY(g0) = -55
    c: Distance(g3) = 80
FEATURE [PartDesign::Pad] Pad016  label="Add stiffening bars to front plate"
  AllowMultiFace = false
  BaseFeature = -> Pocket016
  Direction = (1,1,1)
  Length = 4
  Length2 = 100
  Placement = pos=(0,0,0) rot=(1,0,0;1.5708rad)
  Profile = -> Sketch035
  Type = 0
FEATURE [PartDesign::Fillet] Fillet004
  Base = -> Pad016 [Face119]
  BaseFeature = -> Pad016
  Placement = pos=(0,0,0) rot=(1,0,0;1.5708rad)
  Radius = 0.1
  SupportTransform = false
  UseAllEdges = false
FEATURE [PartDesign::Chamfer] Chamfer016  label="Chamfer hoop"
  Angle = 45
  Base = -> Pad014 [Face4,Face3]
  BaseFeature = -> Pad014
  ChamferType = 0
  FlipDirection = false
  Size = 0.25
  Size2 = 1
  SupportTransform = false
  UseAllEdges = false
FEATURE [PartDesign::Body] Body008  label="Hoop"
  Group = -> [Sketch033,Pad014,Chamfer016]
  Origin = -> Origin012
  Placement = pos=(-12.4,-68.6,34) rot=(0.999924,0.008726,-0.008726;1.57087rad)
  Tip = -> Chamfer016
FEATURE [Part::FeaturePython] Array005  label="Joining bar array"  # Draft array (typed FeaturePython)
  Angle = 360
  ArrayType = 1
  Axis = (0,0,1)
  Base = -> Body007
  Center = (0,0,0)
  Fuse = false
  IntervalAxis = (0,0,0)
  IntervalX = (1,0,0)
  IntervalY = (0,1,0)
  IntervalZ = (0,0,1)
  NumberPolar = 2
  NumberX = 2
  NumberY = 2
  NumberZ = 1
FEATURE [Sketcher::SketchObject] Sketch036  label="top cap profile"
  FullyConstrained = true
  MapMode = 5
  Support = -> [XY_Plane014]
  sketch-geometry (4):
    g0: LineSegment StartX=-63 StartY=70 StartZ=0 EndX=63 EndY=70 EndZ=0
    g1: LineSegment StartX=63 StartY=70 StartZ=0 EndX=63 EndY=-70 EndZ=0
    g2: LineSegment StartX=63 StartY=-70 StartZ=0 EndX=-63 EndY=-70 EndZ=0
    g3: LineSegment StartX=-63 StartY=-70 StartZ=0 EndX=-63 EndY=70 EndZ=0
  constraints (10):
    c: Coincident(g0,g1)
    c: Coincident(g1,g2)
    c: Coincident(g2,g3)
    c: Coincident(g3,g0)
    c: Horizontal(g2)
    c: Vertical(g1)
    c: Symmetric(g0,g0,g-2)
    c: Symmetric(g0,g2,g-1)
    c: Distance(g0) = 126
    c: Distance(g3) = 140
FEATURE [PartDesign::Pad] Pad017  label="Make top cap block"
  AllowMultiFace = false
  Direction = (1,1,1)
  Length = 43
  Length2 = 100
  Profile = -> Sketch036
  Type = 0
FEATURE [PartDesign::Thickness] Thickness  label="Turn block into a shell"
  Base = -> Pad017 [Face5]
  BaseFeature = -> Pad017
  Intersection = false
  Join = 1
  Mode = 0
  Reversed = true
  SupportTransform = false
  Value = 3
FEATURE [PartDesign::Chamfer] Chamfer017  label="Inner corner chamfers"
  Angle = 45
  Base = -> Thickness [Edge22,Edge24,Edge23,Edge17,Edge18,Edge19,Edge21,Edge20]
  BaseFeature = -> Thickness
  ChamferType = 0
  FlipDirection = false
  Size = 2
  Size2 = 1
  SupportTransform = false
  UseAllEdges = false
FEATURE [Sketcher::SketchObject] Sketch037  label="Cap retaining holes spec"
  ExternalGeometry = -> [Chamfer017]
  FullyConstrained = true
  MapMode = 5
  Placement = pos=(-63,0,0) rot=(0.57735,-0.57735,-0.57735;2.0944rad)
  Support = -> [Chamfer017]
  sketch-geometry (2):
    g0: Circle CenterX=-45 CenterY=8 CenterZ=0 NormalX=0 NormalY=0 NormalZ=1 AngleXU=0 Radius=2.25
    g1: Circle CenterX=45 CenterY=8 CenterZ=0 NormalX=0 NormalY=0 NormalZ=1 AngleXU=0 Radius=2.25
  constraints (5):
    c: Symmetric(g0,g1,g-2)
    c: Radius(g0) = 2.25
    c: Equal(g0,g1)
    c: DistanceX(g-3,g0) = 25
    c: DistanceY(g-3,g0) = 8
FEATURE [PartDesign::Pocket] Pocket018  label="Add cap retaining screwholes"
  AllowMultiFace = false
  BaseFeature = -> Chamfer017
  Direction = (1,1,1)
  Length = 5
  Length2 = 100
  Profile = -> Sketch037
  Type = 1
FEATURE [PartDesign::Chamfer] Chamfer018  label="Prettying chamfer"
  Angle = 45
  Base = -> Pocket018 [Face13,Face12,Face11,Face10]
  BaseFeature = -> Pocket018
  ChamferType = 0
  FlipDirection = false
  Size = 1
  Size2 = 1
  SupportTransform = false
  UseAllEdges = false
FEATURE [Sketcher::SketchObject] Sketch038  label="Badge holding holes"
  ExternalGeometry = -> [Chamfer018]
  FullyConstrained = true
  MapMode = 5
  Placement = pos=(0,-70,0) rot=(1,0,0;1.5708rad)
  Support = -> [Chamfer018]
  sketch-geometry (3):
    g0: Circle CenterX=-20 CenterY=21.5 CenterZ=0 NormalX=0 NormalY=0 NormalZ=1 AngleXU=0 Radius=3.3
    g1: Circle CenterX=20 CenterY=21.5 CenterZ=0 NormalX=0 NormalY=0 NormalZ=1 AngleXU=0 Radius=3.3
    g2: LineSegment StartX=-23.3 StartY=21.5 StartZ=0 EndX=-62 EndY=21.5 EndZ=0
  constraints (7):
    c: Radius(g0) = 3.3
    c: Equal(g0,g1)
    c: Distance(g0,g1) = 40
    c: Symmetric(g0,g1,g-2)
    c: Perpendicular(g2,g0) = 1.5708
    c: Perpendicular(g2,g-3) = 4.71239
    c: Symmetric(g-3,g-3,g2)
FEATURE [PartDesign::Pocket] Pocket019  label="Add badge holding holes"
  AllowMultiFace = false
  BaseFeature = -> Chamfer018
  Direction = (1,1,1)
  Length = 5
  Length2 = 100
  Profile = -> Sketch038
  Type = 0
FEATURE [PartDesign::Chamfer] Chamfer019  label="Chamfer badge holding holes"
  Angle = 45
  Base = -> Pocket019 [Face35,Face34]
  BaseFeature = -> Pocket019
  ChamferType = 0
  FlipDirection = false
  Size = 0.3
  Size2 = 1
  SupportTransform = false
  UseAllEdges = false
FEATURE [Sketcher::SketchObject] Sketch039  label="Handle hole spec"
  FullyConstrained = true
  MapMode = 5
  Placement = pos=(0,0,40) rot=(1,0,0;3.14159rad)
  Support = -> [Chamfer019]
  sketch-geometry (2):
    g0: Circle CenterX=0 CenterY=48 CenterZ=0 NormalX=0 NormalY=0 NormalZ=1 AngleXU=0 Radius=2.3
    g1: Circle CenterX=0 CenterY=-48 CenterZ=0 NormalX=0 NormalY=0 NormalZ=1 AngleXU=0 Radius=2.3
  constraints (5):
    c: Symmetric(g1,g0,g-1)
    c: PointOnObject(g0,g-2)
    c: Distance(g0,g1) = 96
    c: Radius(g0) = 2.3
    c: Equal(g0,g1)
FEATURE [PartDesign::Pocket] Pocket020  label="Add handle holes"
  AllowMultiFace = false
  BaseFeature = -> Chamfer019
  Direction = (1,1,1)
  Length = 5
  Length2 = 100
  Profile = -> Sketch039
  Type = 1
FEATURE [PartDesign::Chamfer] Chamfer020  label="Tidy handle holes"
  Angle = 45
  Base = -> Pocket020 [Face41,Face40]
  BaseFeature = -> Pocket020
  ChamferType = 0
  FlipDirection = false
  Size = 0.25
  Size2 = 1
  SupportTransform = false
  UseAllEdges = false
FEATURE [PartDesign::Body] Body009  label="Cap"
  Group = -> [Sketch036,Pad017,Thickness,Chamfer017,Sketch037,Pocket018,Chamfer018,Sketch038,Pocket019,Chamfer019,Sketch039,Pocket020,Chamfer020]
  Origin = -> Origin014
  Tip = -> Chamfer020
FEATURE [App::DocumentObjectGroup] Group003  label="Side Assemblies"
  Group = -> [Part,Part001,Part__Mirroring,Part__Mirroring004,Part__Mirroring003]
FEATURE [Sketcher::SketchObject] Sketch  label="Base tray footprint"
  FullyConstrained = true
  MapMode = 5
  Support = -> [XY_Plane]
  sketch-geometry (4):
    g0: LineSegment StartX=-60 StartY=87.5 StartZ=0 EndX=60 EndY=87.5 EndZ=0
    g1: LineSegment StartX=60 StartY=87.5 StartZ=0 EndX=60 EndY=-87.5 EndZ=0
    g2: LineSegment StartX=60 StartY=-87.5 StartZ=0 EndX=-60 EndY=-87.5 EndZ=0
    g3: LineSegment StartX=-60 StartY=-87.5 StartZ=0 EndX=-60 EndY=87.5 EndZ=0
  constraints (10):
    c: Coincident(g0,g1)
    c: Coincident(g1,g2)
    c: Coincident(g2,g3)
    c: Coincident(g3,g0)
    c: Horizontal(g2)
    c: Vertical(g1)
    c: Symmetric(g0,g0,g-2)
    c: Symmetric(g0,g2,g-1)
    c: Distance(g0) = 120
    c: Distance(g3) = 175
FEATURE [PartDesign::Pad] Pad018  label="Make Basetray"
  Direction = (1,1,1)
  Length = 17
  Length2 = 100
  Profile = -> Sketch
  Type = 0
FEATURE [Sketcher::SketchObject] Sketch042  label="Base Tray Hole pattern"
  ExternalGeometry = -> [Pad018]
  FullyConstrained = true
  MapMode = 5
  Placement = pos=(0,0,17) rot=(0,0,1;0rad)
  Support = -> [Pad018]
  sketch-geometry (11):
    g0: Circle CenterX=-39.425 CenterY=-81.1382 CenterZ=0 NormalX=0 NormalY=0 NormalZ=1 AngleXU=0 Radius=2.2
    g1: Circle CenterX=-39.425 CenterY=-30.2682 CenterZ=0 NormalX=0 NormalY=0 NormalZ=1 AngleXU=0 Radius=2.2
    g2: Circle CenterX=-39.425 CenterY=20.6018 CenterZ=0 NormalX=0 NormalY=0 NormalZ=1 AngleXU=0 Radius=2.2
    g3: Circle CenterX=-39.425 CenterY=72.7458 CenterZ=0 NormalX=0 NormalY=0 NormalZ=1 AngleXU=0 Radius=2.2
    g4: Circle CenterX=39.425 CenterY=72.7458 CenterZ=0 NormalX=0 NormalY=0 NormalZ=1 AngleXU=0 Radius=2.2
    g5: Circle CenterX=39.425 CenterY=20.6018 CenterZ=0 NormalX=0 NormalY=0 NormalZ=1 AngleXU=0 Radius=2.2
    g6: Circle CenterX=39.425 CenterY=-30.2682 CenterZ=0 NormalX=0 NormalY=0 NormalZ=1 AngleXU=0 Radius=2.2
    g7: Circle CenterX=39.425 CenterY=-81.1382 CenterZ=0 NormalX=0 NormalY=0 NormalZ=1 AngleXU=0 Radius=2.2
    g8: LineSegment StartX=-39.425 StartY=-81.1382 StartZ=0 EndX=-39.425 EndY=-30.2682 EndZ=0
    g9: LineSegment StartX=-39.425 StartY=-30.2682 StartZ=0 EndX=-39.425 EndY=20.6018 EndZ=0
    g10: LineSegment StartX=-39.425 StartY=20.6018 StartZ=0 EndX=-39.425 EndY=72.7458 EndZ=0
  constraints (26):
    c: Radius(g0) = 2.2
    c: Equal(g0,g7)
    c: Equal(g0,g1)
    c: Equal(g0,g6)
    c: Equal(g0,g5)
    c: Equal(g0,g2)
    c: Equal(g0,g3)
    c: Equal(g0,g4)
    c: Symmetric(g3,g4,g-2)
    c: Symmetric(g2,g5,g-2)
    c: Symmetric(g1,g6,g-2)
    c: Symmetric(g0,g7,g-2)
    c: Coincident(g8,g9)
    c: Coincident(g9,g10)
    c: Coincident(g10,g3)
    c: Coincident(g9,g2)
    c: Coincident(g8,g1)
    c: Coincident(g0,g8)
    c: DistanceY(g-3,g0) = 6.3618
    c: DistanceX(g0,g7) = 78.85
    c: Vertical(g8)
    c: Vertical(g9)
    c: Vertical(g10)
    c: Distance(g8) = 50.87
    c: Distance(g9) = 50.87
    c: Distance(g10) = 52.144
FEATURE [PartDesign::Pocket] Pocket021  label="Make PCB Mounting Holes"
  BaseFeature = -> Pad018
  Direction = (1,1,1)
  Length = 5
  Length2 = 100
  Profile = -> Sketch042
  Type = 1
FEATURE [Sketcher::SketchObject] Sketch043  label="Center space cutout spec for PCB"
  ExternalGeometry = -> [Pocket021]
  FullyConstrained = true
  MapMode = 5
  Placement = pos=(0,-87.5,0) rot=(1,0,0;1.5708rad)
  Support = -> [Pocket021]
  sketch-geometry (4):
    g0: LineSegment StartX=-50.5 StartY=17 StartZ=0 EndX=50.5 EndY=17 EndZ=0
    g1: LineSegment StartX=50.5 StartY=17 StartZ=0 EndX=50.5 EndY=3 EndZ=0
    g2: LineSegment StartX=50.5 StartY=3 StartZ=0 EndX=-50.5 EndY=3 EndZ=0
    g3: LineSegment StartX=-50.5 StartY=3 StartZ=0 EndX=-50.5 EndY=17 EndZ=0
  constraints (11):
    c: Coincident(g0,g1)
    c: Coincident(g1,g2)
    c: Coincident(g2,g3)
    c: Coincident(g3,g0)
    c: Horizontal(g0)
    c: Vertical(g1)
    c: Vertical(g3)
    c: DistanceY(g-3,g1) = 3
    c: Symmetric(g2,g1,g-2)
    c: DistanceX(g1,g-3) = 9.5
    c: PointOnObject(g0,g-4)
FEATURE [PartDesign::Pocket] Pocket022  label="Make center space for PCB"
  BaseFeature = -> Pocket021
  Direction = (1,1,1)
  Length = 5
  Length2 = 100
  Profile = -> Sketch043
  Type = 1
FEATURE [Sketcher::SketchObject] Sketch044  label="Side panel screwhole spec"
  FullyConstrained = true
  MapMode = 5
  Placement = pos=(-60,0,0) rot=(0.57735,-0.57735,-0.57735;2.0944rad)
  Support = -> [Pocket022]
  sketch-geometry (7):
    g0: Circle CenterX=75 CenterY=10.5 CenterZ=0 NormalX=0 NormalY=0 NormalZ=1 AngleXU=0 Radius=2.2
    g1: Circle CenterX=25 CenterY=10.5 CenterZ=0 NormalX=0 NormalY=0 NormalZ=1 AngleXU=0 Radius=2.2
    g2: Circle CenterX=-25 CenterY=10.5 CenterZ=0 NormalX=0 NormalY=0 NormalZ=1 AngleXU=0 Radius=2.2
    g3: Circle CenterX=-75 CenterY=10.5 CenterZ=0 NormalX=0 NormalY=0 NormalZ=1 AngleXU=0 Radius=2.2
    g4: LineSegment StartX=75 StartY=10.5 StartZ=0 EndX=25 EndY=10.5 EndZ=0
    g5: LineSegment StartX=25 StartY=10.5 StartZ=0 EndX=-25 EndY=10.5 EndZ=0
    g6: LineSegment StartX=-25 StartY=10.5 StartZ=0 EndX=-75 EndY=10.5 EndZ=0
  constraints (17):
    c: Coincident(g4,g5)
    c: Coincident(g5,g6)
    c: Equal(g6,g5)
    c: Equal(g5,g4)
    c: Horizontal(g6)
    c: Horizontal(g4)
    c: Coincident(g6,g3)
    c: Coincident(g5,g2)
    c: Coincident(g4,g1)
    c: Coincident(g4,g0)
    c: Distance(g4) = 50
    c: DistanceY(g0) = 10.5
    c: Symmetric(g3,g0,g-2)
    c: Radius(g3) = 2.2
    c: Equal(g3,g2)
    c: Equal(g3,g1)
    c: Equal(g3,g0)
FEATURE [PartDesign::Pocket] Pocket023  label="Add side panel screwholes"
  BaseFeature = -> Pocket022
  Direction = (1,1,1)
  Length = 5
  Length2 = 100
  Profile = -> Sketch044
  Type = 1
FEATURE [Sketcher::SketchObject] Sketch045  label="Nut trap pocket spec"
  ExternalGeometry = -> [Pocket023]
  FullyConstrained = true
  MapMode = 5
  Placement = pos=(0,0,17) rot=(0,0,1;0rad)
  Support = -> [Pocket023]
  sketch-geometry (18):
    g0: LineSegment StartX=-57 StartY=28.5 StartZ=0 EndX=-53.5 EndY=28.5 EndZ=0
    g1: LineSegment StartX=-53.5 StartY=28.5 StartZ=0 EndX=-53.5 EndY=21.5 EndZ=0
    g2: LineSegment StartX=-53.5 StartY=21.5 StartZ=0 EndX=-57 EndY=21.5 EndZ=0
    g3: LineSegment StartX=-57 StartY=21.5 StartZ=0 EndX=-57 EndY=28.5 EndZ=0
    g4: LineSegment StartX=-57 StartY=-21.5 StartZ=0 EndX=-53.5 EndY=-21.5 EndZ=0
    g5: LineSegment StartX=-53.5 StartY=-21.5 StartZ=0 EndX=-53.5 EndY=-28.5 EndZ=0
    g6: LineSegment StartX=-53.5 StartY=-28.5 StartZ=0 EndX=-57 EndY=-28.5 EndZ=0
    g7: LineSegment StartX=-57 StartY=-28.5 StartZ=0 EndX=-57 EndY=-21.5 EndZ=0
    g8: LineSegment StartX=-57 StartY=-71.5 StartZ=0 EndX=-53.5 EndY=-71.5 EndZ=0
    g9: LineSegment StartX=-53.5 StartY=-71.5 StartZ=0 EndX=-53.5 EndY=-78.5 EndZ=0
    g10: LineSegment StartX=-53.5 StartY=-78.5 StartZ=0 EndX=-57 EndY=-78.5 EndZ=0
    g11: LineSegment StartX=-57 StartY=-78.5 StartZ=0 EndX=-57 EndY=-71.5 EndZ=0
    g12: LineSegment StartX=-57 StartY=78.5 StartZ=0 EndX=-53.5 EndY=78.5 EndZ=0
    g13: LineSegment StartX=-53.5 StartY=78.5 StartZ=0 EndX=-53.5 EndY=71.5 EndZ=0
    g14: LineSegment StartX=-53.5 StartY=71.5 StartZ=0 EndX=-57 EndY=71.5 EndZ=0
    g15: LineSegment StartX=-57 StartY=71.5 StartZ=0 EndX=-57 EndY=78.5 EndZ=0
    g16: LineSegment StartX=-55.25 StartY=87.5 StartZ=0 EndX=-55.25 EndY=78.5 EndZ=0
    g17: LineSegment StartX=-53.5 StartY=71.5 StartZ=0 EndX=-53.5 EndY=28.5 EndZ=0
  constraints (50):
    c: Coincident(g0,g1)
    c: Coincident(g1,g2)
    c: Coincident(g2,g3)
    c: Coincident(g3,g0)
    c: Horizontal(g0)
    c: Horizontal(g2)
    c: Vertical(g1)
    c: Vertical(g3)
    c: Coincident(g4,g5)
    c: Coincident(g5,g6)
    c: Coincident(g6,g7)
    c: Coincident(g7,g4)
    c: Horizontal(g4)
    c: Horizontal(g6)
    c: Vertical(g5)
    c: Vertical(g7)
    c: Coincident(g8,g9)
    c: Coincident(g9,g10)
    c: Coincident(g10,g11)
    c: Coincident(g11,g8)
    c: Horizontal(g8)
    c: Horizontal(g10)
    c: Vertical(g9)
    c: Vertical(g11)
    c: Coincident(g12,g13)
    c: Coincident(g13,g14)
    c: Coincident(g14,g15)
    c: Coincident(g15,g12)
    c: Horizontal(g14)
    c: Vertical(g13)
    c: Vertical(g15)
    c: Equal(g12,g0)
    c: Equal(g0,g4)
    c: Equal(g4,g8)
    c: Equal(g9,g5)
    c: Equal(g5,g13)
    c: Equal(g13,g1)
    c: Distance(g13) = 7
    c: Distance(g12) = 3.5
    c: Symmetric(g-3,g-3,g16)
    c: PointOnObject(g16,g-3)
    c: DistanceY(g0,g12) = 50
    c: Symmetric(g0,g5,g-1)
    c: DistanceY(g5,g1) = 50
    c: Coincident(g17,g13)
    c: Coincident(g17,g0)
    c: Vertical(g17)
    c: Symmetric(g12,g9,g-1)
    c: PointOnObject(g16,g12)
    c: Symmetric(g12,g12,g16)
FEATURE [PartDesign::Pocket] Pocket024  label="Add nut trap pockets"
  BaseFeature = -> Pocket023
  Direction = (1,1,1)
  Length = 10.7
  Length2 = 100
  Profile = -> Sketch045
  Type = 0
FEATURE [PartDesign::Mirrored] Mirrored009  label="Add nut trap pockets to other side"
  BaseFeature = -> Pocket024
  MirrorPlane = -> Sketch045 [V_Axis]
  Originals = -> [Pocket024]
FEATURE [Sketcher::SketchObject] Sketch046  label="Waste material trim tool"
  ExternalGeometry = -> [Mirrored009]
  FullyConstrained = true
  MapMode = 5
  Placement = pos=(0,0,17) rot=(0,0,1;0rad)
  Support = -> [Mirrored009]
  sketch-geometry (20):
    g0: LineSegment StartX=-57 StartY=-81.5 StartZ=0 EndX=-50.5 EndY=-81.5 EndZ=0
    g1: LineSegment StartX=-50.5 StartY=-81.5 StartZ=0 EndX=-50.5 EndY=-87.5 EndZ=0
    g2: LineSegment StartX=-50.5 StartY=-87.5 StartZ=0 EndX=-57 EndY=-87.5 EndZ=0
    g3: LineSegment StartX=-57 StartY=-87.5 StartZ=0 EndX=-57 EndY=-81.5 EndZ=0
    g4: LineSegment StartX=-57 StartY=87.5 StartZ=0 EndX=-50.5 EndY=87.5 EndZ=0
    g5: LineSegment StartX=-50.5 StartY=87.5 StartZ=0 EndX=-50.5 EndY=81.5 EndZ=0
    g6: LineSegment StartX=-50.5 StartY=81.5 StartZ=0 EndX=-57 EndY=81.5 EndZ=0
    g7: LineSegment StartX=-57 StartY=81.5 StartZ=0 EndX=-57 EndY=87.5 EndZ=0
    g8: LineSegment StartX=-57 StartY=68.5 StartZ=0 EndX=-50.5 EndY=68.5 EndZ=0
    g9: LineSegment StartX=-50.5 StartY=68.5 StartZ=0 EndX=-50.5 EndY=31.5 EndZ=0
    g10: LineSegment StartX=-50.5 StartY=31.5 StartZ=0 EndX=-57 EndY=31.5 EndZ=0
    g11: LineSegment StartX=-57 StartY=31.5 StartZ=0 EndX=-57 EndY=68.5 EndZ=0
    g12: LineSegment StartX=-57 StartY=-31.5 StartZ=0 EndX=-50.5 EndY=-31.5 EndZ=0
    g13: LineSegment StartX=-50.5 StartY=-31.5 StartZ=0 EndX=-50.5 EndY=-68.5 EndZ=0
    g14: LineSegment StartX=-50.5 StartY=-68.5 StartZ=0 EndX=-57 EndY=-68.5 EndZ=0
    g15: LineSegment StartX=-57 StartY=-68.5 StartZ=0 EndX=-57 EndY=-31.5 EndZ=0
    g16: LineSegment StartX=-57 StartY=18.5 StartZ=0 EndX=-50.5 EndY=18.5 EndZ=0
    g17: LineSegment StartX=-50.5 StartY=18.5 StartZ=0 EndX=-50.5 EndY=-18.5 EndZ=0
    g18: LineSegment StartX=-50.5 StartY=-18.5 StartZ=0 EndX=-57 EndY=-18.5 EndZ=0
    g19: LineSegment StartX=-57 StartY=-18.5 StartZ=0 EndX=-57 EndY=18.5 EndZ=0
  constraints (56):
    c: Coincident(g0,g1)
    c: Coincident(g1,g2)
    c: Coincident(g2,g3)
    c: Coincident(g3,g0)
    c: Horizontal(g0)
    c: Horizontal(g2)
    c: Vertical(g1)
    c: Vertical(g3)
    c: Coincident(g1,g-3)
    c: DistanceX(g-4,g2) = 3
    c: DistanceY(g0,g-5) = 3
    c: Coincident(g4,g5)
    c: Coincident(g5,g6)
    c: Coincident(g6,g7)
    c: Coincident(g7,g4)
    c: Horizontal(g4)
    c: Horizontal(g6)
    c: Vertical(g5)
    c: Vertical(g7)
    c: Coincident(g4,g-3)
    c: Equal(g5,g1)
    c: Equal(g0,g4)
    c: Coincident(g8,g9)
    c: Coincident(g9,g10)
    c: Coincident(g10,g11)
    c: Coincident(g11,g8)
    c: Horizontal(g8)
    c: Horizontal(g10)
    c: Vertical(g9)
    c: Vertical(g11)
    c: Coincident(g12,g13)
    c: Coincident(g13,g14)
    c: Coincident(g14,g15)
    c: Coincident(g15,g12)
    c: Horizontal(g12)
    c: Horizontal(g14)
    c: Vertical(g13)
    c: Vertical(g15)
    c: Equal(g8,g4)
    c: Equal(g4,g12)
    c: PointOnObject(g8,g-3)
    c: DistanceY(g-7,g10) = 3
    c: DistanceY(g8,g-6) = 3
    c: Equal(g11,g15)
    c: Symmetric(g12,g9,g-1)
    c: Coincident(g16,g17)
    c: Coincident(g17,g18)
    c: Coincident(g18,g19)
    c: Coincident(g19,g16)
    c: Horizontal(g16)
    c: Horizontal(g18)
    c: Vertical(g17)
    c: Equal(g18,g12)
    c: Equal(g17,g13)
    c: PointOnObject(g17,g-3)
    c: Symmetric(g16,g18,g-1)
FEATURE [PartDesign::Pocket] Pocket025  label="Trim waste material from side around nut traps"
  BaseFeature = -> Mirrored009
  Direction = (1,1,1)
  Length = 0
  Length2 = 100
  Profile = -> Sketch046
  Type = 3
  UpToFace = -> Mirrored009 [Face6]
FEATURE [PartDesign::Mirrored] Mirrored010  label="Trim waste material from other side aound nut traps"
  BaseFeature = -> Pocket025
  MirrorPlane = -> Sketch046 [V_Axis]
  Originals = -> [Pocket025]
FEATURE [Sketcher::SketchObject] Sketch047  label="PCB Pillars spec"
  ExternalGeometry = -> [Mirrored010]
  FullyConstrained = true
  MapMode = 5
  Placement = pos=(0,7e-16,3) rot=(0,0,1;0rad)
  Support = -> [Mirrored010]
  sketch-geometry (9):
    g0: LineSegment StartX=-39.425 StartY=70.5458 StartZ=0 EndX=-39.425 EndY=68.0458 EndZ=0
    g1: Circle CenterX=-39.425 CenterY=-81.1382 CenterZ=0 NormalX=0 NormalY=0 NormalZ=1 AngleXU=0 Radius=2.2
    g2: Circle CenterX=-39.425 CenterY=-30.2682 CenterZ=0 NormalX=0 NormalY=0 NormalZ=1 AngleXU=0 Radius=2.2
    g3: Circle CenterX=-39.425 CenterY=20.6018 CenterZ=0 NormalX=0 NormalY=0 NormalZ=1 AngleXU=0 Radius=2.2
    g4: Circle CenterX=-39.425 CenterY=72.7458 CenterZ=0 NormalX=0 NormalY=0 NormalZ=1 AngleXU=0 Radius=2.2
    g5: Circle CenterX=-39.425 CenterY=72.7458 CenterZ=0 NormalX=0 NormalY=0 NormalZ=1 AngleXU=0 Radius=4.7
    g6: Circle CenterX=-39.425 CenterY=20.6018 CenterZ=0 NormalX=0 NormalY=0 NormalZ=1 AngleXU=0 Radius=4.7
    g7: Circle CenterX=-39.425 CenterY=-30.2682 CenterZ=0 NormalX=0 NormalY=0 NormalZ=1 AngleXU=0 Radius=4.7
    g8: Circle CenterX=-39.425 CenterY=-81.1382 CenterZ=0 NormalX=0 NormalY=0 NormalZ=1 AngleXU=0 Radius=4.7
  constraints (19):
    c: Vertical(g0)
    c: Distance(g0) = 2.5
    c: Coincident(g-3,g4)
    c: Coincident(g-4,g3)
    c: Coincident(g-5,g2)
    c: Coincident(g-6,g1)
    c: Equal(g1,g2)
    c: Equal(g2,g3)
    c: Equal(g3,g4)
    c: Equal(g4,g-3)
    c: Perpendicular(g0,g4) = 1.5708
    c: Coincident(g1,g8)
    c: Coincident(g2,g7)
    c: Coincident(g6,g3)
    c: PointOnObject(g0,g5)
    c: Coincident(g4,g5)
    c: Equal(g6,g5)
    c: Equal(g5,g7)
    c: Equal(g7,g8)
FEATURE [PartDesign::Pad] Pad019  label="Make PCB Pillars down one side"
  BaseFeature = -> Mirrored010
  Direction = (1,1,1)
  Length = 5
  Length2 = 100
  Profile = -> Sketch047
  Type = 0
FEATURE [PartDesign::Mirrored] Mirrored011  label="Add PCB Pillars to other side"
  BaseFeature = -> Pad019
  MirrorPlane = -> Sketch047 [V_Axis]
  Originals = -> [Pad019]
FEATURE [Part::Part2DObjectPython] ShapeString  label="Shapestring 'Top'"  # Draft 2D object (typed FeaturePython)
  FontFile = <userpath>/USERROOT/Fonts/impact.ttf
  Placement = pos=(-15,66,3) rot=(0,0,1;0rad)
  Size = 16
  String = Top
  Tracking = 0
FEATURE [PartDesign::Pocket] Pocket026  label="Add 'Top' to tray"
  BaseFeature = -> Mirrored011
  Direction = (1,1,1)
  Length = 1.5
  Length2 = 100
  Profile = -> ShapeString
  Type = 0
FEATURE [PartDesign::Chamfer] Chamfer  label="Nut trap lead-in chamfer"
  Angle = 45
  Base = -> Pocket026 [Edge163,Edge164,Edge166,Edge165,Edge170,Edge168,Edge167,Edge169,Edge159,Edge160,Edge161,Edge162,Edge155,Edge156,Edge158,Edge157,Edge48,Edge47,Edge52,Edge51,Edge60,Edge59,Edge56,Edge55,Edge57,Edge54,Edge61,Edge58,Edge53,Edge50,Edge49,Edge46]
  BaseFeature = -> Pocket026
  ChamferType = 0
  FlipDirection = false
  Size = 0.5
  Size2 = 1
  SupportTransform = false
  UseAllEdges = false
FEATURE [PartDesign::Chamfer] Chamfer021  label="Print aide bottom hole chamfers"
  Angle = 45
  Base = -> Pocket026 [Edge21,Edge20,Edge17,Edge16,Edge15,Edge14,Edge19,Edge18]
  BaseFeature = -> Pocket026
  ChamferType = 0
  FlipDirection = false
  Size = 0.5
  Size2 = 1
  SupportTransform = false
  UseAllEdges = false
FEATURE [PartDesign::Body] Body  label="V3 Basetray"
  Group = -> [Sketch,Pad018,Sketch042,Pocket021,Sketch043,Pocket022,Sketch044,Pocket023,Sketch045,Pocket024,Mirrored009,Sketch046,Pocket025,Mirrored010,Sketch047,Pad019,Mirrored011,ShapeString,Pocket026,Chamfer,Chamfer021]
  Origin = -> Origin
  Placement = pos=(0,0,0) rot=(0,0,1;1.5708rad)
  Tip = -> Chamfer021
FEATURE [PartDesign::Chamfer] Chamfer022
  Angle = 45
  Base = -> Pad013 [Edge15,Edge11]
  BaseFeature = -> Pad013
  ChamferType = 0
  FlipDirection = false
  Placement = pos=(0,0,0) rot=(1,0,0;1.5708rad)
  Size = 1
  Size2 = 1
  SupportTransform = false
  UseAllEdges = false
FEATURE [PartDesign::Body] Body002  label="LH Side plate"
  Group = -> [Sketch002,Pad001,Sketch003,Pad002,Mirrored,Sketch004,Pocket,Mirrored001,Sketch015,Pocket006,Mirrored003,Sketch016,Pocket007,Sketch017,Pocket008,LinearPattern,Chamfer001,Chamfer006,Sketch032,Pad013,Chamfer022]
  Origin = -> Origin006
  Tip = -> Chamfer022
FEATURE [Part::FeaturePython] Array003  label="Sideplate array"  # Draft array (typed FeaturePython)
  Angle = 360
  ArrayType = 1
  Axis = (0,0,1)
  Base = -> Body002
  Center = (0,0,0)
  Fuse = false
  IntervalAxis = (0,0,0)
  IntervalX = (1,0,0)
  IntervalY = (0,1,0)
  IntervalZ = (0,0,1)
  NumberPolar = 2
  NumberX = 2
  NumberY = 2
  NumberZ = 1
FEATURE [PartDesign::ShapeBinder] ShapeBinder  label="Hole in cap shape-binder"
  Support = -> [Chamfer020]
  TraceSupport = false
FEATURE [Sketcher::SketchObject] Sketch048  label="Badge-plate spec"
  ExternalGeometry = -> [ShapeBinder]
  FullyConstrained = true
  MapMode = 5
  Placement = pos=(0,0,0) rot=(1,0,0;1.5708rad)
  Support = -> [XZ_Plane018]
  sketch-geometry (5):
    g0: LineSegment StartX=-47.5 StartY=34 StartZ=0 EndX=47.5 EndY=34 EndZ=0
    g1: LineSegment StartX=47.5 StartY=34 StartZ=0 EndX=47.5 EndY=9 EndZ=0
    g2: LineSegment StartX=47.5 StartY=9 StartZ=0 EndX=-47.5 EndY=9 EndZ=0
    g3: LineSegment StartX=-47.5 StartY=9 StartZ=0 EndX=-47.5 EndY=34 EndZ=0
    g4: LineSegment StartX=-47.5 StartY=21.5 StartZ=0 EndX=-20 EndY=21.5 EndZ=0
  constraints (13):
    c: Coincident(g0,g1)
    c: Coincident(g1,g2)
    c: Coincident(g2,g3)
    c: Coincident(g3,g0)
    c: Horizontal(g2)
    c: Vertical(g1)
    c: Vertical(g3)
    c: Coincident(g4,g-3)
    c: Perpendicular(g4,g3) = 1.5708
    c: Symmetric(g2,g0,g4)
    c: Symmetric(g0,g0,g-2)
    c: Distance(g1) = 25
    c: Distance(g0) = 95
FEATURE [PartDesign::Pad] Pad020  label="Make badge plate"
  Direction = (1,1,1)
  Length = 2.5
  Length2 = 100
  Placement = pos=(0,0,0) rot=(1,0,0;1.5708rad)
  Profile = -> Sketch048
  Type = 0
FEATURE [Sketcher::SketchObject] Sketch049  label="Mounting lugs spec"
  ExternalGeometry = -> [Pad020,ShapeBinder]
  FullyConstrained = true
  MapMode = 5
  Placement = pos=(0,0,0) rot=(-1,0,0;1.5708rad)
  Support = -> [Pad020]
  sketch-geometry (3):
    g0: Circle CenterX=-20 CenterY=-21.5 CenterZ=0 NormalX=0 NormalY=0 NormalZ=1 AngleXU=0 Radius=3.05
    g1: Circle CenterX=20 CenterY=-21.5 CenterZ=0 NormalX=0 NormalY=0 NormalZ=1 AngleXU=0 Radius=3.05
    g2: LineSegment StartX=-20 StartY=-18.2 StartZ=0 EndX=-20 EndY=-18.45 EndZ=0
  constraints (7):
    c: Symmetric(g0,g1,g-2)
    c: Equal(g0,g1)
    c: Perpendicular(g2,g-4) = 4.71239
    c: Vertical(g2)
    c: PointOnObject(g2,g0)
    c: Distance(g2) = 0.25
    c: Coincident(g-4,g0)
FEATURE [PartDesign::Pad] Pad021  label="Make mounting lugs"
  BaseFeature = -> Pad020
  Direction = (1,1,1)
  Length = 5
  Length2 = 100
  Placement = pos=(0,0,0) rot=(1,0,0;1.5708rad)
  Profile = -> Sketch049
  Type = 0
FEATURE [Sketcher::SketchObject] Sketch050  label="Badge frame cut spec"
  ExternalGeometry = -> [Pad021]
  FullyConstrained = true
  MapMode = 5
  Placement = pos=(0,0,0) rot=(-1,0,0;1.5708rad)
  Support = -> [Pad021]
  sketch-geometry (9):
    g0: LineSegment StartX=-47.5 StartY=-9 StartZ=0 EndX=47.5 EndY=-9 EndZ=0
    g1: LineSegment StartX=47.5 StartY=-9 StartZ=0 EndX=47.5 EndY=-34 EndZ=0
    g2: LineSegment StartX=47.5 StartY=-34 StartZ=0 EndX=-47.5 EndY=-34 EndZ=0
    g3: LineSegment StartX=-47.5 StartY=-34 StartZ=0 EndX=-47.5 EndY=-9 EndZ=0
    g4: LineSegment StartX=-44.75 StartY=-11.75 StartZ=0 EndX=44.75 EndY=-11.75 EndZ=0
    g5: LineSegment StartX=44.75 StartY=-11.75 StartZ=0 EndX=44.75 EndY=-31.25 EndZ=0
    g6: LineSegment StartX=44.75 StartY=-31.25 StartZ=0 EndX=-44.75 EndY=-31.25 EndZ=0
    g7: LineSegment StartX=-44.75 StartY=-31.25 StartZ=0 EndX=-44.75 EndY=-11.75 EndZ=0
    g8: LineSegment StartX=-44.75 StartY=-21.5 StartZ=0 EndX=-47.5 EndY=-21.5 EndZ=0
  constraints (22):
    c: Coincident(g0,g1)
    c: Coincident(g1,g2)
    c: Coincident(g2,g3)
    c: Coincident(g3,g0)
    c: Horizontal(g2)
    c: Vertical(g1)
    c: Coincident(g4,g5)
    c: Coincident(g5,g6)
    c: Coincident(g6,g7)
    c: Coincident(g7,g4)
    c: Horizontal(g6)
    c: Vertical(g5)
    c: Symmetric(g0,g0,g-2)
    c: Symmetric(g4,g4,g-2)
    c: PointOnObject(g8,g-3)
    c: Symmetric(g-3,g-3,g8)
    c: PointOnObject(g8,g7)
    c: Symmetric(g6,g4,g8)
    c: Coincident(g0,g-3)
    c: Symmetric(g2,g0,g8)
    c: DistanceY(g4,g0) = 2.75
    c: DistanceX(g0,g4) = 2.75
FEATURE [PartDesign::Pocket] Pocket027  label="Add badge frame cut"
  BaseFeature = -> Pad021
  Direction = (1,1,1)
  Length = 1.25
  Length2 = 100
  Placement = pos=(0,0,0) rot=(1,0,0;1.5708rad)
  Profile = -> Sketch050
  Type = 0
FEATURE [PartDesign::Body] Body010  label="Badge"
  Group = -> [Sketch048,ShapeBinder,Pad020,Sketch049,Pad021,Sketch050,Pocket027]
  Origin = -> Origin018
  Placement = pos=(0,-70.15,0) rot=(0,0,1;0rad)
  Tip = -> Pocket027
FEATURE [PartDesign::ShapeBinder] ShapeBinder001  label="Badge back shapebinder"
  Placement = pos=(0,0,0) rot=(1,0,0;1.5708rad)
  Support = -> [Pocket027]
  TraceSupport = false
FEATURE [Sketcher::SketchObject] Sketch051  label="Badge Frame retaining lip spec"
  ExternalGeometry = -> [ShapeBinder001]
  FullyConstrained = true
  MapMode = 5
  Placement = pos=(0,0,0) rot=(1,0,0;1.5708rad)
  Support = -> [XZ_Plane020]
  sketch-geometry (12):
    g0: LineSegment StartX=-44.9 StartY=11.6 StartZ=0 EndX=44.9 EndY=11.6 EndZ=0
    g1: LineSegment StartX=44.9 StartY=11.6 StartZ=0 EndX=44.9 EndY=31.4 EndZ=0
    g2: LineSegment StartX=44.9 StartY=31.4 StartZ=0 EndX=-44.9 EndY=31.4 EndZ=0
    g3: LineSegment StartX=-44.9 StartY=31.4 StartZ=0 EndX=-44.9 EndY=11.6 EndZ=0
    g4: LineSegment StartX=-50.35 StartY=6.15 StartZ=0 EndX=50.35 EndY=6.15 EndZ=0
    g5: LineSegment StartX=50.35 StartY=6.15 StartZ=0 EndX=50.35 EndY=36.85 EndZ=0
    g6: LineSegment StartX=50.35 StartY=36.85 StartZ=0 EndX=-50.35 EndY=36.85 EndZ=0
    g7: LineSegment StartX=-50.35 StartY=36.85 StartZ=0 EndX=-50.35 EndY=6.15 EndZ=0
    g8: LineSegment StartX=44.9 StartY=31.4 StartZ=0 EndX=44.75 EndY=31.25 EndZ=0
    g9: LineSegment StartX=47.5 StartY=34 StartZ=0 EndX=50.35 EndY=36.85 EndZ=0
    g10: LineSegment StartX=-44.9 StartY=11.6 StartZ=0 EndX=-44.75 EndY=11.75 EndZ=0
    g11: LineSegment StartX=-47.5 StartY=9 StartZ=0 EndX=-50.35 EndY=6.15 EndZ=0
  constraints (32):
    c: Coincident(g0,g1)
    c: Coincident(g1,g2)
    c: Coincident(g2,g3)
    c: Coincident(g3,g0)
    c: Horizontal(g0)
    c: Horizontal(g2)
    c: Vertical(g1)
    c: Vertical(g3)
    c: Coincident(g4,g5)
    c: Coincident(g5,g6)
    c: Coincident(g6,g7)
    c: Coincident(g7,g4)
    c: Horizontal(g4)
    c: Horizontal(g6)
    c: Vertical(g5)
    c: Vertical(g7)
    c: Coincident(g-5,g11)
    c: Coincident(g11,g4)
    c: Coincident(g10,g0)
    c: Coincident(g10,g-6)
    c: Coincident(g9,g5)
    c: Coincident(g9,g-4)
    c: Coincident(g-3,g8)
    c: Coincident(g8,g1)
    c: Angle(g2,g8) = 0.785398
    c: Angle(g6,g9) = 0.785398
    c: Angle(g11,g7) = 0.785398
    c: Angle(g10,g3) = 0.785398
    c: Equal(g11,g9)
    c: Equal(g8,g10)
    c: DistanceY(g0,g10) = 0.15
    c: DistanceY(g4,g11) = 2.85
FEATURE [PartDesign::Pad] Pad022  label="Make badge retaining lip"
  Direction = (1,1,1)
  Length = 1.25
  Length2 = 100
  Placement = pos=(0,0,0) rot=(1,0,0;1.5708rad)
  Profile = -> Sketch051
  Type = 0
FEATURE [Sketcher::SketchObject] Sketch052  label="Badge frame spec"
  ExternalGeometry = -> [Pad022]
  FullyConstrained = true
  MapMode = 5
  Placement = pos=(0,-1.25,3e-16) rot=(1,0,0;1.5708rad)
  Support = -> [Pad022]
  sketch-geometry (10):
    g0: LineSegment StartX=-50.35 StartY=36.85 StartZ=0 EndX=50.35 EndY=36.85 EndZ=0
    g1: LineSegment StartX=50.35 StartY=36.85 StartZ=0 EndX=50.35 EndY=6.15 EndZ=0
    g2: LineSegment StartX=50.35 StartY=6.15 StartZ=0 EndX=-50.35 EndY=6.15 EndZ=0
    g3: LineSegment StartX=-50.35 StartY=6.15 StartZ=0 EndX=-50.35 EndY=36.85 EndZ=0
    g4: LineSegment StartX=-48 StartY=34.5 StartZ=0 EndX=48 EndY=34.5 EndZ=0
    g5: LineSegment StartX=48 StartY=34.5 StartZ=0 EndX=48 EndY=8.5 EndZ=0
    g6: LineSegment StartX=48 StartY=8.5 StartZ=0 EndX=-48 EndY=8.5 EndZ=0
    g7: LineSegment StartX=-48 StartY=8.5 StartZ=0 EndX=-48 EndY=34.5 EndZ=0
    g8: LineSegment StartX=-50.35 StartY=36.85 StartZ=0 EndX=-48 EndY=34.5 EndZ=0
    g9: LineSegment StartX=48 StartY=8.5 StartZ=0 EndX=50.35 EndY=6.15 EndZ=0
  constraints (26):
    c: Coincident(g0,g1)
    c: Coincident(g1,g2)
    c: Coincident(g2,g3)
    c: Coincident(g3,g0)
    c: Horizontal(g0)
    c: Horizontal(g2)
    c: Vertical(g1)
    c: Vertical(g3)
    c: Coincident(g4,g5)
    c: Coincident(g5,g6)
    c: Coincident(g6,g7)
    c: Coincident(g7,g4)
    c: Horizontal(g4)
    c: Horizontal(g6)
    c: Vertical(g5)
    c: Vertical(g7)
    c: Coincident(g1,g-4)
    c: Coincident(g0,g-3)
    c: Coincident(g9,g1)
    c: Coincident(g9,g5)
    c: Coincident(g8,g4)
    c: Coincident(g8,g0)
    c: Angle(g8,g0) = 0.785398
    c: Parallel(g8,g9)
    c: Equal(g9,g8)
    c: DistanceY(g4,g0) = 2.35
FEATURE [PartDesign::Pad] Pad023  label="Make Badge frame"
  BaseFeature = -> Pad022
  Direction = (1,1,1)
  Length = 3.75
  Length2 = 100
  Placement = pos=(0,0,0) rot=(1,0,0;1.5708rad)
  Profile = -> Sketch052
  Type = 0
FEATURE [PartDesign::Fillet] Fillet  label="Badge frame outer radius"
  Base = -> Pad023 [Edge20,Edge17,Edge22,Edge16]
  BaseFeature = -> Pad023
  Placement = pos=(0,0,0) rot=(1,0,0;1.5708rad)
  Radius = 1
  SupportTransform = false
  UseAllEdges = false
FEATURE [PartDesign::Fillet] Fillet005  label="Badge frame front edge chafer"
  Base = -> Fillet [Edge22]
  BaseFeature = -> Fillet
  Placement = pos=(0,0,0) rot=(1,0,0;1.5708rad)
  Radius = 0.5
  SupportTransform = false
  UseAllEdges = false
FEATURE [PartDesign::Body] Body011  label="Badge Frame"
  Group = -> [ShapeBinder001,Sketch051,Pad022,Sketch052,Pad023,Fillet,Fillet005]
  Origin = -> Origin020
  Placement = pos=(0,-70,0) rot=(0,0,1;0rad)
  Tip = -> Fillet005
FEATURE [App::Part] Part005  label="Badge Assy"
  Group = -> [Body010,Body011]
  Origin = -> Origin019
FEATURE [App::Part] Part003  label="Final top cap assembly"
  Group = -> [Body009,Part005]
  Origin = -> Origin016
  Placement = pos=(-87.65,0,70) rot=(0.57735,0.57735,-0.57735;4.18879rad)
FEATURE [Sketcher::SketchObject] Sketch053  label="Bottom card clearance cut tool"
  ExternalGeometry = -> [Fillet004]
  FullyConstrained = true
  MapMode = 5
  Placement = pos=(0,-3,-7e-16) rot=(1,0,0;1.5708rad)
  Support = -> [Fillet004]
  sketch-geometry (4):
    g0: LineSegment StartX=-45.5 StartY=68 StartZ=0 EndX=45.5 EndY=68 EndZ=0
    g1: LineSegment StartX=45.5 StartY=68 StartZ=0 EndX=45.5 EndY=66 EndZ=0
    g2: LineSegment StartX=45.5 StartY=66 StartZ=0 EndX=-45.5 EndY=66 EndZ=0
    g3: LineSegment StartX=-45.5 StartY=66 StartZ=0 EndX=-45.5 EndY=68 EndZ=0
  constraints (11):
    c: Coincident(g0,g1)
    c: Coincident(g1,g2)
    c: Coincident(g2,g3)
    c: Coincident(g3,g0)
    c: Horizontal(g2)
    c: Vertical(g1)
    c: Vertical(g3)
    c: Distance(g3) = 2
    c: Symmetric(g0,g0,g-2)
    c: PointOnObject(g0,g-3)
    c: DistanceX(g-4,g2) = 17.5
FEATURE [PartDesign::Pocket] Pocket028  label="Add bottom card clearance cut"
  BaseFeature = -> Fillet004
  Direction = (1,1,1)
  Length = 5
  Length2 = 100
  Placement = pos=(0,0,0) rot=(1,0,0;1.5708rad)
  Profile = -> Sketch053
  Type = 1
FEATURE [Sketcher::SketchObject] Sketch054  label="Larger rocker cutout spec"
  ExternalGeometry = -> [Pocket028]
  FullyConstrained = true
  MapMode = 5
  Placement = pos=(0,-3,-7e-16) rot=(1,0,0;1.5708rad)
  Support = -> [Pocket028]
  sketch-geometry (6):
    g0: LineSegment StartX=-43 StartY=49.3 StartZ=0 EndX=-31.4 EndY=49.3 EndZ=0
    g1: LineSegment StartX=-31.4 StartY=49.3 StartZ=0 EndX=-31.4 EndY=18.7 EndZ=0
    g2: LineSegment StartX=-31.4 StartY=18.7 StartZ=0 EndX=-43 EndY=18.7 EndZ=0
    g3: LineSegment StartX=-43 StartY=18.7 StartZ=0 EndX=-43 EndY=49.3 EndZ=0
    g4: LineSegment StartX=-37.2 StartY=43.925 StartZ=0 EndX=-37.2 EndY=49.3 EndZ=0
    g5: LineSegment StartX=-41.025 StartY=34 StartZ=0 EndX=-43 EndY=34 EndZ=0
  constraints (16):
    c: Coincident(g0,g1)
    c: Coincident(g1,g2)
    c: Coincident(g2,g3)
    c: Coincident(g3,g0)
    c: Horizontal(g2)
    c: Vertical(g1)
    c: Perpendicular(g5,g-4) = 4.71239
    c: Perpendicular(g4,g-3) = 4.71239
    c: PointOnObject(g4,g0)
    c: PointOnObject(g5,g3)
    c: Symmetric(g0,g2,g5)
    c: Symmetric(g0,g0,g4)
    c: Symmetric(g-4,g-3,g4)
    c: Symmetric(g-4,g-4,g5)
    c: Distance(g1) = 30.6
    c: Distance(g0) = 11.6
FEATURE [PartDesign::Pocket] Pocket029  label="Add larger rocker cutout"
  BaseFeature = -> Pocket028
  Direction = (1,1,1)
  Length = 5
  Length2 = 100
  Placement = pos=(0,0,0) rot=(1,0,0;1.5708rad)
  Profile = -> Sketch054
  Type = 1
FEATURE [Sketcher::SketchObject] Sketch055  label="Switch clip cutout spec"
  ExternalGeometry = -> [Pocket029]
  FullyConstrained = true
  MapMode = 5
  Placement = pos=(0,-1e-16,0) rot=(-1,0,0;1.5708rad)
  Support = -> [Pocket029]
  sketch-geometry (4):
    g0: LineSegment StartX=-43 StartY=-15.7 StartZ=0 EndX=-31.4 EndY=-15.7 EndZ=0
    g1: LineSegment StartX=-31.4 StartY=-15.7 StartZ=0 EndX=-31.4 EndY=-52.3 EndZ=0
    g2: LineSegment StartX=-31.4 StartY=-52.3 StartZ=0 EndX=-43 EndY=-52.3 EndZ=0
    g3: LineSegment StartX=-43 StartY=-52.3 StartZ=0 EndX=-43 EndY=-15.7 EndZ=0
  constraints (12):
    c: Coincident(g0,g1)
    c: Coincident(g1,g2)
    c: Coincident(g2,g3)
    c: Coincident(g3,g0)
    c: Horizontal(g0)
    c: Horizontal(g2)
    c: Vertical(g1)
    c: Vertical(g3)
    c: PointOnObject(g-3,g3)
    c: PointOnObject(g-4,g1)
    c: Distance(g1,g-4) = 3
    c: Distance(g-4,g0) = 3
FEATURE [PartDesign::Pocket] Pocket030  label="Add clip cutouts for larger rocker switch"
  BaseFeature = -> Pocket029
  Direction = (1,1,1)
  Length = 1.25
  Length2 = 100
  Placement = pos=(0,0,0) rot=(1,0,0;1.5708rad)
  Profile = -> Sketch055
  Type = 0
FEATURE [PartDesign::Body] Body004  label="Front Endplate"
  Group = -> [Sketch011,Pad006,Sketch012,Pad007,Mirrored002,Sketch013,Pocket004,Sketch014,Pocket005,Chamfer004,Chamfer005,Chamfer008,Sketch024,Mirrored005,Pocket012,Sketch025,Pocket013,Chamfer010,Sketch026,Pocket014,Chamfer011,Chamfer012,Sketch030,Pad012,Sketch031,Pocket016,Sketch035,Pad016,Fillet004,Sketch053,Pocket028,Sketch054,Pocket029,Sketch055,Pocket030]
  Origin = -> Origin008
  Placement = pos=(0,-66.95,0) rot=(0,0,1;0rad)
  Tip = -> Pocket030
FEATURE [App::Part] Part002  label="Final bottom cap assembly"
  Group = -> [Body008,Body005,Array003,Body002,Array005,Body007,Array004,Body006,Body004,Body003,Body001]
  Origin = -> Origin013
  Placement = pos=(155.65,0,70) rot=(-0.57735,-0.57735,0.57735;2.0944rad)
FEATURE [App::DocumentObjectGroup] Group002  label="Endcaps"
  Group = -> [Part003,Part002]
FEATURE [App::Part] Part004  label="Entire Assembly"
  Group = -> [Part003,Part002,Part__Feature005,Array001,Part__Mirroring004,Part,Part001,Part__Feature006,Part__Mirroring,Part__Feature004,Array,Part__Mirroring003,Part__Feature001,Part__Mirroring001,Group002,Group003,Body]
  Origin = -> Origin017
  Placement = pos=(0,0,0) rot=(-0.57735,-0.57735,0.57735;4.18879rad)
FEATURE [Sketcher::SketchObject] Sketch056  label="Faceplate front spec"
  FullyConstrained = true
  MapMode = 5
  Support = -> [XY_Plane021]
  sketch-geometry (6):
    g0: LineSegment StartX=-63 StartY=12.5 StartZ=0 EndX=63 EndY=12.5 EndZ=0
    g1: LineSegment StartX=63 StartY=12.5 StartZ=0 EndX=63 EndY=-12.5 EndZ=0
    g2: LineSegment StartX=63 StartY=-12.5 StartZ=0 EndX=-63 EndY=-12.5 EndZ=0
    g3: LineSegment StartX=-63 StartY=-12.5 StartZ=0 EndX=-63 EndY=12.5 EndZ=0
    g4: Circle CenterX=-53 CenterY=0.726 CenterZ=0 NormalX=0 NormalY=0 NormalZ=1 AngleXU=0 Radius=2.2
    g5: Circle CenterX=53 CenterY=0.726 CenterZ=0 NormalX=0 NormalY=0 NormalZ=1 AngleXU=0 Radius=2.2
  constraints (16):
    c: Coincident(g0,g1)
    c: Coincident(g1,g2)
    c: Coincident(g2,g3)
    c: Coincident(g3,g0)
    c: Horizontal(g0)
    c: Horizontal(g2)
    c: Vertical(g1)
    c: Vertical(g3)
    c: Symmetric(g2,g0,g-1)
    c: Distance(g3) = 25
    c: Distance(g0) = 126
    c: Symmetric(g4,g5,g-2)
    c: DistanceY(g4,g0) = 11.774
    c: Equal(g4,g5)
    c: Radius(g4) = 2.2
    c: DistanceX(g4,g5) = 106
FEATURE [PartDesign::Pad] Pad024  label="Make faceplate front blank"
  Direction = (0,0,1)
  Length = 3
  Length2 = 10
  Profile = -> Sketch056
  ReferenceAxis = -> Sketch056 [N_Axis]
  Type = 0
FEATURE [Sketcher::SketchObject] Sketch057  label="Tab footprint spec"
  ExternalGeometry = -> [Pad024]
  FullyConstrained = true
  MapMode = 5
  Placement = pos=(0,0,3) rot=(0,0,1;0rad)
  Support = -> [Pad024]
  sketch-geometry (8):
    g0: LineSegment StartX=-44.354 StartY=-1.892 StartZ=0 EndX=-31.954 EndY=-1.892 EndZ=0
    g1: LineSegment StartX=-31.954 StartY=-1.892 StartZ=0 EndX=-31.954 EndY=-5.892 EndZ=0
    g2: LineSegment StartX=-31.954 StartY=-5.892 StartZ=0 EndX=-44.354 EndY=-5.892 EndZ=0
    g3: LineSegment StartX=-44.354 StartY=-5.892 StartZ=0 EndX=-44.354 EndY=-1.892 EndZ=0
    g4: LineSegment StartX=31.954 StartY=-1.892 StartZ=0 EndX=44.354 EndY=-1.892 EndZ=0
    g5: LineSegment StartX=44.354 StartY=-1.892 StartZ=0 EndX=44.354 EndY=-5.892 EndZ=0
    g6: LineSegment StartX=44.354 StartY=-5.892 StartZ=0 EndX=31.954 EndY=-5.892 EndZ=0
    g7: LineSegment StartX=31.954 StartY=-5.892 StartZ=0 EndX=31.954 EndY=-1.892 EndZ=0
  constraints (23):
    c: Coincident(g0,g1)
    c: Coincident(g1,g2)
    c: Coincident(g2,g3)
    c: Coincident(g3,g0)
    c: Horizontal(g0)
    c: Horizontal(g2)
    c: Vertical(g1)
    c: Vertical(g3)
    c: Coincident(g4,g5)
    c: Coincident(g5,g6)
    c: Coincident(g6,g7)
    c: Coincident(g7,g4)
    c: Horizontal(g4)
    c: Horizontal(g6)
    c: Vertical(g5)
    c: Vertical(g7)
    c: Equal(g1,g7)
    c: Equal(g0,g4)
    c: Distance(g0) = 12.4
    c: Distance(g3) = 4
    c: Symmetric(g0,g4,g-2)
    c: DistanceX(g2,g6) = 76.308
    c: DistanceY(g2,g-3) = 18.392
FEATURE [PartDesign::Pad] Pad025  label="Make tab"
  BaseFeature = -> Pad024
  Direction = (0,0,1)
  Length = 21.5
  Length2 = 10
  Profile = -> Sketch057
  ReferenceAxis = -> Sketch057 [N_Axis]
  Type = 0
FEATURE [Sketcher::SketchObject] Sketch058  label="Board mounting screwhole spec"
  ExternalGeometry = -> [Pad025]
  FullyConstrained = true
  MapMode = 5
  Placement = pos=(0,-1.892,0) rot=(0,0.707107,0.707107;3.14159rad)
  Support = -> [Pad025]
  sketch-geometry (2):
    g0: Circle CenterX=-38.154 CenterY=18.3 CenterZ=0 NormalX=0 NormalY=0 NormalZ=1 AngleXU=0 Radius=2.2
    g1: Circle CenterX=38.154 CenterY=18.3 CenterZ=0 NormalX=0 NormalY=0 NormalZ=1 AngleXU=0 Radius=2.2
  constraints (5):
    c: Symmetric(g0,g1,g-2)
    c: Radius(g1) = 2.2
    c: DistanceY(g-3,g0) = 15.3
    c: DistanceX(g0,g1) = 76.308
    c: Equal(g0,g1)
FEATURE [PartDesign::Pocket] Pocket031  label="Add board mounting screwholes"
  BaseFeature = -> Pad025
  Direction = (0,-1,2e-16)
  Length = 5
  Length2 = 5
  Profile = -> Sketch058
  ReferenceAxis = -> Sketch058 [N_Axis]
  Type = 1
FEATURE [PartDesign::Chamfer] Chamfer023  label="Add front face chamfer"
  Angle = 45
  Base = -> Pocket031 [Face4]
  BaseFeature = -> Pocket031
  ChamferType = 0
  FlipDirection = false
  Size = 1
  Size2 = 1
  SupportTransform = false
  UseAllEdges = false
FEATURE [PartDesign::Body] Body012  label="Faceplate blank"
  Group = -> [Sketch056,Pad024,Sketch057,Pad025,Sketch058,Pocket031,Chamfer023]
  Origin = -> Origin021
  Placement = pos=(0,-143.1,-77.85) rot=(0,0.707107,0.707107;3.14159rad)
  Tip = -> Chamfer023
FEATURE [Sketcher::SketchObject] Sketch059  label="Faceplate front spec001"
  FullyConstrained = true
  MapMode = 5
  Support = -> [XY_Plane022]
  sketch-geometry (6):
    g0: LineSegment StartX=-70 StartY=12.5 StartZ=0 EndX=70 EndY=12.5 EndZ=0
    g1: LineSegment StartX=70 StartY=12.5 StartZ=0 EndX=70 EndY=-12.5 EndZ=0
    g2: LineSegment StartX=70 StartY=-12.5 StartZ=0 EndX=-70 EndY=-12.5 EndZ=0
    g3: LineSegment StartX=-70 StartY=-12.5 StartZ=0 EndX=-70 EndY=12.5 EndZ=0
    g4: Circle CenterX=-53 CenterY=0.726 CenterZ=0 NormalX=0 NormalY=0 NormalZ=1 AngleXU=0 Radius=2.2
    g5: Circle CenterX=53 CenterY=0.726 CenterZ=0 NormalX=0 NormalY=0 NormalZ=1 AngleXU=0 Radius=2.2
  constraints (16):
    c: Coincident(g0,g1)
    c: Coincident(g1,g2)
    c: Coincident(g2,g3)
    c: Coincident(g3,g0)
    c: Horizontal(g0)
    c: Horizontal(g2)
    c: Vertical(g1)
    c: Vertical(g3)
    c: Symmetric(g2,g0,g-1)
    c: Distance(g3) = 25
    c: Distance(g0) = 140
    c: Symmetric(g4,g5,g-2)
    c: DistanceY(g4,g0) = 11.774
    c: Equal(g4,g5)
    c: Radius(g4) = 2.2
    c: DistanceX(g4,g5) = 106
FEATURE [PartDesign::Pad] Pad026  label="Make faceplate front blank001"
  Direction = (0,0,1)
  Length = 6.5
  Length2 = 10
  Profile = -> Sketch059
  ReferenceAxis = -> Sketch059 [N_Axis]
  Type = 0
FEATURE [Sketcher::SketchObject] Sketch060  label="Tab footprint spec001"
  ExternalGeometry = -> [Pad026]
  FullyConstrained = true
  MapMode = 5
  Placement = pos=(0,0,6.5) rot=(0,0,1;0rad)
  Support = -> [Pad026]
  sketch-geometry (8):
    g0: LineSegment StartX=-44.354 StartY=-1.892 StartZ=0 EndX=-31.954 EndY=-1.892 EndZ=0
    g1: LineSegment StartX=-31.954 StartY=-1.892 StartZ=0 EndX=-31.954 EndY=-5.892 EndZ=0
    g2: LineSegment StartX=-31.954 StartY=-5.892 StartZ=0 EndX=-44.354 EndY=-5.892 EndZ=0
    g3: LineSegment StartX=-44.354 StartY=-5.892 StartZ=0 EndX=-44.354 EndY=-1.892 EndZ=0
    g4: LineSegment StartX=31.954 StartY=-1.892 StartZ=0 EndX=44.354 EndY=-1.892 EndZ=0
    g5: LineSegment StartX=44.354 StartY=-1.892 StartZ=0 EndX=44.354 EndY=-5.892 EndZ=0
    g6: LineSegment StartX=44.354 StartY=-5.892 StartZ=0 EndX=31.954 EndY=-5.892 EndZ=0
    g7: LineSegment StartX=31.954 StartY=-5.892 StartZ=0 EndX=31.954 EndY=-1.892 EndZ=0
  constraints (23):
    c: Coincident(g0,g1)
    c: Coincident(g1,g2)
    c: Coincident(g2,g3)
    c: Coincident(g3,g0)
    c: Horizontal(g0)
    c: Horizontal(g2)
    c: Vertical(g1)
    c: Vertical(g3)
    c: Coincident(g4,g5)
    c: Coincident(g5,g6)
    c: Coincident(g6,g7)
    c: Coincident(g7,g4)
    c: Horizontal(g4)
    c: Horizontal(g6)
    c: Vertical(g5)
    c: Vertical(g7)
    c: Equal(g1,g7)
    c: Equal(g0,g4)
    c: Distance(g0) = 12.4
    c: Distance(g3) = 4
    c: Symmetric(g0,g4,g-2)
    c: DistanceX(g2,g6) = 76.308
    c: DistanceY(g2,g-3) = 18.392
FEATURE [PartDesign::Pad] Pad027  label="Make tab001"
  BaseFeature = -> Pad026
  Direction = (0,0,1)
  Length = 21.5
  Length2 = 10
  Profile = -> Sketch060
  ReferenceAxis = -> Sketch060 [N_Axis]
  Type = 0
FEATURE [Sketcher::SketchObject] Sketch061  label="Board mounting screwhole spec001"
  ExternalGeometry = -> [Pad027]
  FullyConstrained = true
  MapMode = 5
  Placement = pos=(0,-1.892,0) rot=(0,0.707107,0.707107;3.14159rad)
  Support = -> [Pad027]
  sketch-geometry (2):
    g0: Circle CenterX=-38.154 CenterY=21.8 CenterZ=0 NormalX=0 NormalY=0 NormalZ=1 AngleXU=0 Radius=2.2
    g1: Circle CenterX=38.154 CenterY=21.8 CenterZ=0 NormalX=0 NormalY=0 NormalZ=1 AngleXU=0 Radius=2.2
  constraints (5):
    c: Symmetric(g0,g1,g-2)
    c: Radius(g1) = 2.2
    c: DistanceY(g-3,g0) = 15.3
    c: DistanceX(g0,g1) = 76.308
    c: Equal(g0,g1)
FEATURE [PartDesign::Pocket] Pocket032  label="Add board mounting screwholes001"
  BaseFeature = -> Pad027
  Direction = (0,-1,2e-16)
  Length = 5
  Length2 = 5
  Profile = -> Sketch061
  ReferenceAxis = -> Sketch061 [N_Axis]
  Type = 1
FEATURE [PartDesign::Chamfer] Chamfer024  label="Add front face chamfer001"
  Angle = 45
  Base = -> Pocket032 [Face4]
  BaseFeature = -> Pocket032
  ChamferType = 0
  FlipDirection = false
  Size = 1
  Size2 = 1
  SupportTransform = false
  UseAllEdges = false
FEATURE [PartDesign::Body] Body013  label="Card Extender Faceplate"
  Group = -> [Sketch059,Pad026,Sketch060,Pad027,Sketch061,Pocket032,Chamfer024]
  Origin = -> Origin022
  Placement = pos=(0,-145.15,0) rot=(0,-0.707107,-0.707107;3.14159rad)
  Tip = -> Chamfer024
